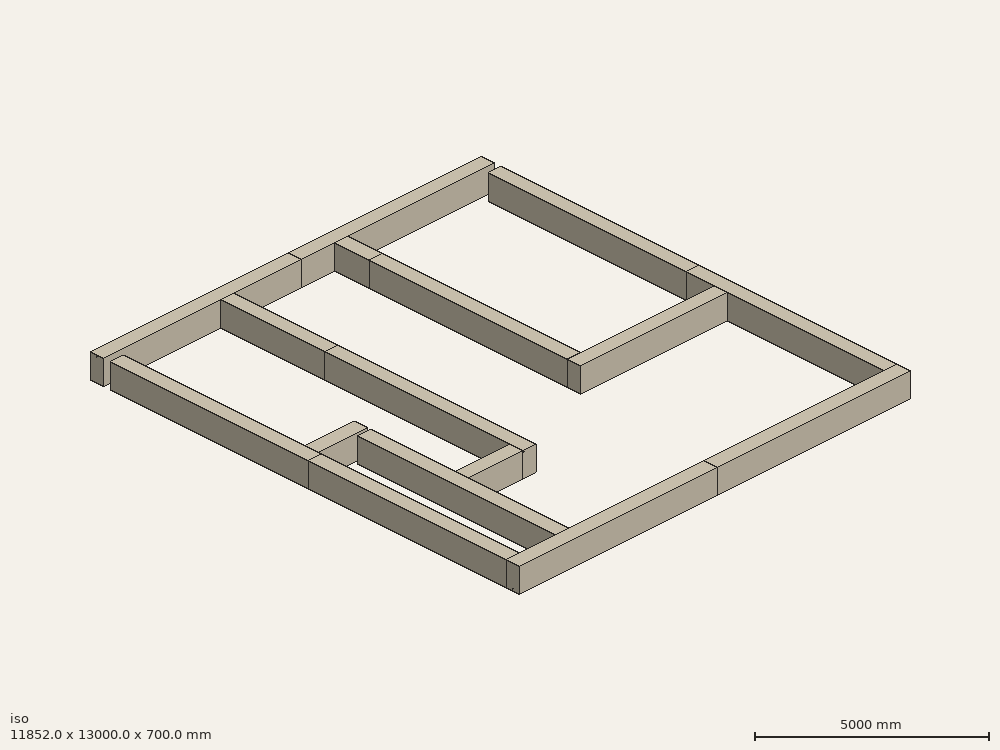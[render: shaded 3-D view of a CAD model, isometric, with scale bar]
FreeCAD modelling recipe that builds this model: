
FCSTD DOCUMENT  (FreeCAD 0.21R33668 +26 (Git))
Label: арматура
License: All rights reserved
objects: Part::FeaturePython×64, Sketcher::SketchObject×33, Part::Box×16, Part::Part2DObjectPython×16, Spreadsheet::Sheet×1
note: 129 computed .brp shape members not serialized (recipe doc carries the construction recipe); baked Part::Feature solids carry a one-line shape summary decoded from their .brp

FEATURE [Part::Box] Box  label="Куб"
  AttacherType = Attacher::AttachEngine3D
  Height = 700
  Length = 6000
  Width = 400
FEATURE [Part::FeaturePython] Structure  label="Структура"  # Arch/BIM 13 (typed FeaturePython)
  Base = -> Box
  BaseMirror = false
  BaseOffsetX = 0
  BaseOffsetY = 0
  BasePerpendicularToTool = false
  BaseRotation = 0
  ComputedLength = 0
  FaceMaker = 0
  Height = 4901.77
  HorizontalArea = 2400000
  IfcData = attributes={"GlobalId": {"name": "GlobalId", "type": "IfcGloballyUniqueId", "is_enum": false, "enum_values": []}, "Description": {"... (+484 chars omitted),+1 more (map truncated)
  IfcType = 13
  Length = 0
  MoveBase = false
  MoveWithHost = false
  NodesOffset = 0
  Normal = (0,0,0)
  PerimeterLength = 12800
  PredefinedType = 0
  ToolOffsetFirst = 0
  ToolOffsetLast = 0
  VerticalArea = 8960000
  Width = 500
FEATURE [Sketcher::SketchObject] Sketch
  FullyConstrained = false
  MapMode = 5
  Placement = pos=(0,0,0) rot=(1,0,0;1.5708rad)
  Support = -> [Structure]
  sketch-geometry (1):
    g0: LineSegment StartX=0 StartY=56 StartZ=0 EndX=6000 EndY=56 EndZ=0
FEATURE [Part::FeaturePython] Rebar  label="Нижняя_рабочая"  # Arch/BIM 110 (typed FeaturePython)
  Amount = 3
  AmountCheck = true
  Base = -> Sketch
  Cover = 50
  CoverAlong = Bottom Side
  Diameter = 12
  Direction = (0,0,0)
  Distance = 0
  FrontCover = 35
  HorizontalArea = 0
  Host = -> Structure
  IfcType = 110
  LeftBottomCover = 0
  Length = 6000
  Mark = StraightRebar
  MoveBase = false
  MoveWithHost = false
  OffsetEnd = 41
  OffsetStart = 41
  Orientation = Horizontal
  PerimeterLength = 0
  PlacementList = 3 placements: arithmetic series from (0,41,-9.10383e-15) step (0,159,-3.53051e-14) to (0,359,-7.9714e-14)
  RebarShape = 0
  RightTopCover = 0
  Rounding = 0
  Spacing = 159
  TotalLength = 18000
  TrueSpacing = 3
  VerticalArea = 0
FEATURE [Sketcher::SketchObject] Sketch001
  FullyConstrained = false
  MapMode = 5
  Placement = pos=(0,0,0) rot=(1,0,0;1.5708rad)
  Support = -> [Structure]
  sketch-geometry (1):
    g0: LineSegment StartX=0 StartY=659 StartZ=0 EndX=6000 EndY=659 EndZ=0
FEATURE [Part::FeaturePython] Rebar001  label="Верхняя_рабочая"  # Arch/BIM 110 (typed FeaturePython)
  Amount = 3
  AmountCheck = true
  Base = -> Sketch001
  Cover = 35
  CoverAlong = Top Side
  Diameter = 12
  Direction = (0,0,0)
  Distance = 0
  FrontCover = 35
  HorizontalArea = 0
  Host = -> Structure
  IfcType = 110
  LeftBottomCover = 0
  Length = 6000
  Mark = StraightRebar001
  MoveBase = false
  MoveWithHost = false
  OffsetEnd = 41
  OffsetStart = 41
  Orientation = Horizontal
  PerimeterLength = 0
  PlacementList = 3 placements: arithmetic series from (0,41,-9.10383e-15) step (0,159,-3.53051e-14) to (0,359,-7.9714e-14)
  RebarShape = 0
  RightTopCover = 0
  Rounding = 0
  Spacing = 159
  TotalLength = 18000
  TrueSpacing = 3
  VerticalArea = 0
FEATURE [Part::Part2DObjectPython] Wire  # Draft 2D object (typed FeaturePython)
  Area = 0
  ChamferSize = 0
  Closed = false
  End = (-10.6616,56.3137,621.059)
  FilletRadius = 0
  Length = 2124.59
  MakeFace = true
  Points = (7) [(2.13232,78.9411,643.686),(0,29,693.627),(-2.13232,29,44),(-4.26465,371,44),(-6.39697,371,671),(-8.5293,6.37258,671),(-10.6616,56.3137,621.059)]
  Start = (2.13232,78.9411,643.686)
  Subdivisions = 0
  Support = -> [Structure]
FEATURE [Part::FeaturePython] Rebar002  label="Хомуты"  # Arch/BIM 110 (typed FeaturePython)
  Amount = 13
  AmountCheck = false
  Base = -> Wire
  BentAngle = 135
  BentFactor = 4
  BottomCover = 40
  Diameter = 8
  Direction = (1,0,0)
  Distance = 0
  FrontCover = 80
  HorizontalArea = 0
  Host = -> Structure
  IfcType = 110
  LeftCover = 25
  Length = 2124.59
  Mark = Stirrup
  MoveBase = false
  MoveWithHost = false
  OffsetEnd = 84
  OffsetStart = 84
  PerimeterLength = 0
  PlacementList = 13 placements: arithmetic series from (84,0,0) step (485.333,0,0) to (5908,0,0)
  RebarShape = 3
  RightCover = 25
  Rounding = 2
  Spacing = 485.333
  TopCover = 25
  TotalLength = 27619.7
  TrueSpacing = 500
  VerticalArea = 0
FEATURE [Sketcher::SketchObject] Sketch003  label="контур_фундамента"
  FullyConstrained = true
  sketch-geometry (40):
    g0: LineSegment StartX=0 StartY=400 StartZ=0 EndX=11850 EndY=400 EndZ=0
    g1: LineSegment StartX=11850 StartY=400 StartZ=0 EndX=11850 EndY=0 EndZ=0
    g2: LineSegment StartX=11850 StartY=0 StartZ=0 EndX=0 EndY=0 EndZ=0
    g3: LineSegment StartX=0 StartY=0 StartZ=0 EndX=0 EndY=400 EndZ=0
    g4: LineSegment StartX=11850 StartY=13000 StartZ=0 EndX=11450 EndY=13000 EndZ=0
    g5: LineSegment StartX=11450 StartY=13000 StartZ=0 EndX=11450 EndY=0 EndZ=0
    g6: LineSegment StartX=11450 StartY=0 StartZ=0 EndX=11850 EndY=0 EndZ=0
    g7: LineSegment StartX=11850 StartY=0 StartZ=0 EndX=11850 EndY=13000 EndZ=0
    g8: LineSegment StartX=8.527e-13 StartY=13000 StartZ=0 EndX=11850 EndY=13000 EndZ=0
    g9: LineSegment StartX=11850 StartY=13000 StartZ=0 EndX=11850 EndY=12600 EndZ=0
    g10: LineSegment StartX=11850 StartY=12600 StartZ=0 EndX=0 EndY=12600 EndZ=0
    g11: LineSegment StartX=8.527e-13 StartY=12600 StartZ=0 EndX=8.527e-13 EndY=13000 EndZ=0
    g12: LineSegment StartX=8.527e-13 StartY=13000 StartZ=0 EndX=400 EndY=13000 EndZ=0
    g13: LineSegment StartX=400 StartY=13000 StartZ=0 EndX=400 EndY=1.819e-12 EndZ=0
    g14: LineSegment StartX=400 StartY=1.819e-12 StartZ=0 EndX=8.527e-13 EndY=1.819e-12 EndZ=0
    g15: LineSegment StartX=8.527e-13 StartY=1.819e-12 StartZ=0 EndX=8.527e-13 EndY=13000 EndZ=0
    g16: LineSegment StartX=3550 StartY=13000 StartZ=0 EndX=3950 EndY=13000 EndZ=0
    g17: LineSegment StartX=3950 StartY=13000 StartZ=0 EndX=3950 EndY=3450 EndZ=0
    g18: LineSegment StartX=3950 StartY=3450 StartZ=0 EndX=3550 EndY=3450 EndZ=0
    g19: LineSegment StartX=3550 StartY=3450 StartZ=0 EndX=3550 EndY=13000 EndZ=0
    g20: LineSegment StartX=9.095e-13 StartY=6900 StartZ=0 EndX=1900 EndY=6900 EndZ=0
    g21: LineSegment StartX=1900 StartY=6900 StartZ=0 EndX=1900 EndY=6500 EndZ=0
    g22: LineSegment StartX=1900 StartY=6500 StartZ=0 EndX=9.095e-13 EndY=6500 EndZ=0
    g23: LineSegment StartX=9.095e-13 StartY=6500 StartZ=0 EndX=9.095e-13 EndY=6900 EndZ=0
    g24: LineSegment StartX=1500 StartY=6900 StartZ=0 EndX=1900 EndY=6900 EndZ=0
    g25: LineSegment StartX=1900 StartY=6900 StartZ=0 EndX=1900 EndY=0 EndZ=0
    g26: LineSegment StartX=1900 StartY=0 StartZ=0 EndX=1500 EndY=0 EndZ=0
    g27: LineSegment StartX=1500 StartY=0 StartZ=0 EndX=1500 EndY=6900 EndZ=0
    g28: LineSegment StartX=1900 StartY=3850 StartZ=0 EndX=3950 EndY=3850 EndZ=0
    g29: LineSegment StartX=3950 StartY=3850 StartZ=0 EndX=3950 EndY=3450 EndZ=0
    g30: LineSegment StartX=3950 StartY=3450 StartZ=0 EndX=1900 EndY=3450 EndZ=0
    g31: LineSegment StartX=1900 StartY=3450 StartZ=0 EndX=1900 EndY=3850 EndZ=0
    g32: LineSegment StartX=7000 StartY=13000 StartZ=0 EndX=7400 EndY=13000 EndZ=0
    g33: LineSegment StartX=7400 StartY=13000 StartZ=0 EndX=7400 EndY=5150 EndZ=0
    g34: LineSegment StartX=7400 StartY=5150 StartZ=0 EndX=7000 EndY=5150 EndZ=0
    g35: LineSegment StartX=7000 StartY=5150 StartZ=0 EndX=7000 EndY=13000 EndZ=0
    g36: LineSegment StartX=7000 StartY=5550 StartZ=0 EndX=11450 EndY=5550 EndZ=0
    g37: LineSegment StartX=11450 StartY=5550 StartZ=0 EndX=11450 EndY=5150 EndZ=0
    g38: LineSegment StartX=11450 StartY=5150 StartZ=0 EndX=7000 EndY=5150 EndZ=0
    g39: LineSegment StartX=7000 StartY=5150 StartZ=0 EndX=7000 EndY=5550 EndZ=0
  constraints (113):
    c: Coincident(g0,g1)
    c: Coincident(g1,g2)
    c: Coincident(g2,g3)
    c: Coincident(g3,g0)
    c: Horizontal(g0)
    c: Horizontal(g2)
    c: Vertical(g1)
    c: Vertical(g3)
    c: DistanceX(g2,g2) = 11850
    c: DistanceY(g1,g1) = 400
    c: Coincident(g2,g-1)
    c: Coincident(g4,g5)
    c: Coincident(g5,g6)
    c: Coincident(g6,g7)
    c: Coincident(g7,g4)
    c: Horizontal(g4)
    c: Horizontal(g6)
    c: Vertical(g5)
    c: Vertical(g7)
    c: DistanceX(g6,g6) = 400
    c: DistanceY(g5,g5) = 13000
    c: Coincident(g6,g1)
    c: Coincident(g8,g9)
    c: Coincident(g9,g10)
    c: Coincident(g10,g11)
    c: Coincident(g11,g8)
    c: Horizontal(g8)
    c: Horizontal(g10)
    c: Vertical(g9)
    c: Vertical(g11)
    c: DistanceY(g9,g9) = 400
    c: DistanceX(g8,g8) = 11850
    c: Coincident(g8,g4)
    c: Coincident(g12,g13)
    c: Coincident(g13,g14)
    c: Coincident(g14,g15)
    c: Coincident(g15,g12)
    c: Horizontal(g12)
    c: Horizontal(g14)
    c: Vertical(g13)
    c: Vertical(g15)
    c: DistanceX(g12,g12) = 400
    c: DistanceY(g15,g15) = 13000
    c: Coincident(g12,g8)
    c: Coincident(g16,g17)
    c: Coincident(g17,g18)
    c: Coincident(g18,g19)
    c: Coincident(g19,g16)
    c: Horizontal(g16)
    c: Horizontal(g18)
    c: Vertical(g17)
    c: Vertical(g19)
    c: DistanceX(g16,g16) = 400
    c: DistanceX(g8,g16) = 3950
    c: DistanceY(g17,g8) = 9550
    c: DistanceY(g19,g19) = 9550
    c: Coincident(g20,g21)
    c: Coincident(g21,g22)
    c: Coincident(g22,g23)
    c: Coincident(g23,g20)
    c: Horizontal(g20)
    c: Horizontal(g22)
    c: Vertical(g21)
    c: Vertical(g23)
    c: DistanceX(g20,g20) = 1900
    c: DistanceY(g23,g23) = 400
    c: DistanceY(g22,g8) = 6500
    c: DistanceX(g8,g20) = 1900
    c: Coincident(g24,g25)
    c: Coincident(g25,g26)
    c: Coincident(g26,g27)
    c: Coincident(g27,g24)
    c: Horizontal(g24)
    c: Horizontal(g26)
    c: Vertical(g25)
    c: Vertical(g27)
    c: DistanceX(g24,g24) = 400
    c: DistanceY(g25,g25) = 6900
    c: Coincident(g24,g20)
    c: Coincident(g28,g29)
    c: Coincident(g29,g30)
    c: Coincident(g30,g31)
    c: Coincident(g31,g28)
    c: Horizontal(g28)
    c: Horizontal(g30)
    c: Vertical(g29)
    c: Vertical(g31)
    c: DistanceY(g29,g29) = 400
    c: DistanceX(g28,g28) = 2050
    c: Coincident(g17,g29)
    c: Coincident(g32,g33)
    c: Coincident(g33,g34)
    c: Coincident(g34,g35)
    c: Coincident(g35,g32)
    c: Horizontal(g32)
    c: Horizontal(g34)
    c: Vertical(g33)
    c: Vertical(g35)
    c: DistanceX(g32,g32) = 400
    c: DistanceY(g33,g33) = 7850
    c: DistanceX(g32,g4) = 4850
    c: DistanceY(g33,g4) = 7850
    c: Coincident(g36,g37)
    c: Coincident(g37,g38)
    c: Coincident(g38,g39)
    c: Coincident(g39,g36)
    c: Horizontal(g36)
    c: Horizontal(g38)
    c: Vertical(g37)
    c: Vertical(g39)
    c: DistanceY(g39,g39) = 400
    c: DistanceX(g38,g38) = 4450
    c: Coincident(g38,g34)
FEATURE [Part::Box] Box001  label="Куб001"
  AttacherType = Attacher::AttachEngine3D
  Height = 700
  Length = 5850
  Width = 400
FEATURE [Part::FeaturePython] Structure001  label="Структура001"  # Arch/BIM 13 (typed FeaturePython)
  Base = -> Box001
  BaseMirror = false
  BaseOffsetX = 0
  BaseOffsetY = 0
  BasePerpendicularToTool = false
  BaseRotation = 0
  ComputedLength = 0
  FaceMaker = 0
  Height = 345.39
  HorizontalArea = 2340000
  IfcData = attributes={"GlobalId": {"name": "GlobalId", "type": "IfcGloballyUniqueId", "is_enum": false, "enum_values": []}, "Description": {"... (+484 chars omitted),+1 more (map truncated)
  IfcType = 13
  Length = 0
  MoveBase = false
  MoveWithHost = false
  NodesOffset = 0
  Normal = (0,0,0)
  PerimeterLength = 12500
  Placement = pos=(6001,0,0) rot=(0,0,1;0rad)
  PredefinedType = 0
  ToolOffsetFirst = 0
  ToolOffsetLast = 0
  VerticalArea = 8750000
  Width = 100
FEATURE [Sketcher::SketchObject] Sketch004
  FullyConstrained = false
  MapMode = 5
  Placement = pos=(6001,0,0) rot=(1,0,0;1.5708rad)
  Support = -> [Structure001]
  sketch-geometry (1):
    g0: LineSegment StartX=0 StartY=56 StartZ=0 EndX=5850 EndY=56 EndZ=0
FEATURE [Part::FeaturePython] Rebar004  label="Нижняя_рабочая001"  # Arch/BIM 110 (typed FeaturePython)
  Amount = 3
  AmountCheck = true
  Base = -> Sketch004
  Cover = 50
  CoverAlong = Bottom Side
  Diameter = 12
  Direction = (0,0,0)
  Distance = 0
  FrontCover = 35
  HorizontalArea = 0
  Host = -> Structure001
  IfcType = 110
  LeftBottomCover = 0
  Length = 5850
  Mark = StraightRebar
  MoveBase = false
  MoveWithHost = false
  OffsetEnd = 41
  OffsetStart = 41
  Orientation = Horizontal
  PerimeterLength = 0
  PlacementList = 3 placements: arithmetic series from (0,41,-9.10383e-15) step (0,159,-3.53051e-14) to (0,359,-7.9714e-14)
  RebarShape = 0
  RightTopCover = 0
  Rounding = 0
  Spacing = 159
  TotalLength = 17550
  TrueSpacing = 3
  VerticalArea = 0
FEATURE [Sketcher::SketchObject] Sketch005
  FullyConstrained = false
  MapMode = 5
  Placement = pos=(6001,0,0) rot=(1,0,0;1.5708rad)
  Support = -> [Structure001]
  sketch-geometry (1):
    g0: LineSegment StartX=0 StartY=659 StartZ=0 EndX=5850 EndY=659 EndZ=0
FEATURE [Part::FeaturePython] Rebar005  label="Верхняя_рабочая001"  # Arch/BIM 110 (typed FeaturePython)
  Amount = 3
  AmountCheck = true
  Base = -> Sketch005
  Cover = 35
  CoverAlong = Top Side
  Diameter = 12
  Direction = (0,0,0)
  Distance = 0
  FrontCover = 35
  HorizontalArea = 0
  Host = -> Structure001
  IfcType = 110
  LeftBottomCover = 0
  Length = 5850
  Mark = StraightRebar
  MoveBase = false
  MoveWithHost = false
  OffsetEnd = 41
  OffsetStart = 41
  Orientation = Horizontal
  PerimeterLength = 0
  PlacementList = 3 placements: arithmetic series from (0,41,-9.10383e-15) step (0,159,-3.53051e-14) to (0,359,-7.9714e-14)
  RebarShape = 0
  RightTopCover = 0
  Rounding = 0
  Spacing = 159
  TotalLength = 17550
  TrueSpacing = 3
  VerticalArea = 0
FEATURE [Part::Part2DObjectPython] Wire001  # Draft 2D object (typed FeaturePython)
  Area = 0
  ChamferSize = 0
  Closed = false
  End = (11840.3,56.3137,621.059)
  FilletRadius = 0
  Length = 2124.59
  MakeFace = true
  Points = (7) [(11853.1,78.9411,643.686),(11851,29,693.627),(11848.9,29,44),(11846.7,371,44),(11844.6,371,671),(11842.5,6.37258,671),(11840.3,56.3137,621.059)]
  Start = (11853.1,78.9411,643.686)
  Subdivisions = 0
  Support = -> [Structure001]
FEATURE [Part::FeaturePython] Rebar007  label="Хомуты001"  # Arch/BIM 110 (typed FeaturePython)
  Amount = 13
  AmountCheck = false
  Base = -> Wire001
  BentAngle = 135
  BentFactor = 4
  BottomCover = 40
  Diameter = 8
  Direction = (-1,0,0)
  Distance = 0
  FrontCover = 80
  HorizontalArea = 0
  Host = -> Structure001
  IfcType = 110
  LeftCover = 25
  Length = 2124.59
  Mark = Stirrup
  MoveBase = false
  MoveWithHost = false
  OffsetEnd = 84
  OffsetStart = 84
  PerimeterLength = 0
  PlacementList = 13 placements: arithmetic series from (-84,0,0) step (-472.833,0,0) to (-5758,0,0)
  RebarShape = 3
  RightCover = 25
  Rounding = 2
  Spacing = 472.833
  TopCover = 25
  TotalLength = 27619.7
  TrueSpacing = 500
  VerticalArea = 0
FEATURE [Part::Box] Box002  label="Куб002"
  AttacherType = Attacher::AttachEngine3D
  Height = 700
  Length = 6000
  Width = 400
FEATURE [Part::FeaturePython] Structure002  label="Структура002"  # Arch/BIM 13 (typed FeaturePython)
  Base = -> Box002
  BaseMirror = false
  BaseOffsetX = 0
  BaseOffsetY = 0
  BasePerpendicularToTool = false
  BaseRotation = 0
  ComputedLength = 0
  FaceMaker = 0
  Height = 1000
  HorizontalArea = 2400000
  IfcData = attributes={"GlobalId": {"name": "GlobalId", "type": "IfcGloballyUniqueId", "is_enum": false, "enum_values": []}, "Description": {"... (+484 chars omitted),+1 more (map truncated)
  IfcType = 13
  Length = 0
  MoveBase = false
  MoveWithHost = false
  NodesOffset = 0
  Normal = (0,0,0)
  PerimeterLength = 12800
  Placement = pos=(399,403,0) rot=(0,0,1;1.5708rad)
  PredefinedType = 0
  ToolOffsetFirst = 0
  ToolOffsetLast = 0
  VerticalArea = 8960000
  Width = 100
FEATURE [Sketcher::SketchObject] Sketch007
  FullyConstrained = false
  MapMode = 5
  Placement = pos=(-1,403,0) rot=(-0.57735,0.57735,0.57735;4.18879rad)
  Support = -> [Structure002]
  sketch-geometry (1):
    g0: LineSegment StartX=-6000 StartY=56 StartZ=0 EndX=0 EndY=56 EndZ=0
FEATURE [Part::FeaturePython] Rebar008  label="Нижняя_рабочая002"  # Arch/BIM 110 (typed FeaturePython)
  Amount = 3
  AmountCheck = true
  Base = -> Sketch007
  Cover = 50
  CoverAlong = Bottom Side
  Diameter = 12
  Direction = (0,0,0)
  Distance = 0
  FrontCover = 35
  HorizontalArea = 0
  Host = -> Structure002
  IfcType = 110
  LeftBottomCover = 0
  Length = 6000
  Mark = StraightRebar
  MoveBase = false
  MoveWithHost = false
  OffsetEnd = 41
  OffsetStart = 41
  Orientation = Horizontal
  PerimeterLength = 0
  PlacementList = 3 placements: arithmetic series from (41,-4.55191e-15,-4.55191e-15) step (159,-1.76525e-14,-1.76525e-14) to (359,-3.9857e-14,-3.9857e-14)
  RebarShape = 0
  RightTopCover = 0
  Rounding = 0
  Spacing = 159
  TotalLength = 18000
  TrueSpacing = 3
  VerticalArea = 0
FEATURE [Sketcher::SketchObject] Sketch008
  FullyConstrained = false
  MapMode = 5
  Placement = pos=(-1,403,0) rot=(-0.57735,0.57735,0.57735;4.18879rad)
  Support = -> [Structure002]
  sketch-geometry (1):
    g0: LineSegment StartX=-6000 StartY=659 StartZ=0 EndX=0 EndY=659 EndZ=0
FEATURE [Part::FeaturePython] Rebar009  label="Верхняя_рабочая002"  # Arch/BIM 110 (typed FeaturePython)
  Amount = 3
  AmountCheck = true
  Base = -> Sketch008
  Cover = 35
  CoverAlong = Top Side
  Diameter = 12
  Direction = (0,0,0)
  Distance = 0
  FrontCover = 35
  HorizontalArea = 0
  Host = -> Structure002
  IfcType = 110
  LeftBottomCover = 0
  Length = 6000
  Mark = StraightRebar
  MoveBase = false
  MoveWithHost = false
  OffsetEnd = 41
  OffsetStart = 41
  Orientation = Horizontal
  PerimeterLength = 0
  PlacementList = 3 placements: arithmetic series from (41,-4.55191e-15,-4.55191e-15) step (159,-1.76525e-14,-1.76525e-14) to (359,-3.9857e-14,-3.9857e-14)
  RebarShape = 0
  RightTopCover = 0
  Rounding = 0
  Spacing = 159
  TotalLength = 18000
  TrueSpacing = 3
  VerticalArea = 0
FEATURE [Part::Part2DObjectPython] Wire002  # Draft 2D object (typed FeaturePython)
  Area = 0
  ChamferSize = 0
  Closed = false
  End = (55.3137,6392.34,621.059)
  FilletRadius = 0
  Length = 2124.59
  MakeFace = true
  Points = (7) [(77.9411,6405.13,643.686),(28,6403,693.627),(28,6400.87,44),(370,6398.74,44),(370,6396.6,671),(5.37258,6394.47,671),(55.3137,6392.34,621.059)]
  Start = (77.9411,6405.13,643.686)
  Subdivisions = 0
  Support = -> [Structure002]
FEATURE [Part::FeaturePython] Rebar011  label="Хомуты002"  # Arch/BIM 110 (typed FeaturePython)
  Amount = 13
  AmountCheck = false
  Base = -> Wire002
  BentAngle = 135
  BentFactor = 4
  BottomCover = 40
  Diameter = 8
  Direction = (-2e-16,-1,0)
  Distance = 0
  FrontCover = 80
  HorizontalArea = 0
  Host = -> Structure002
  IfcType = 110
  LeftCover = 25
  Length = 2124.59
  Mark = Stirrup
  MoveBase = false
  MoveWithHost = false
  OffsetEnd = 84
  OffsetStart = 84
  PerimeterLength = 0
  PlacementList = 13 placements: arithmetic series from (-1.86517e-14,-84,0) step (-1.07766e-13,-485.333,0) to (-1.31184e-12,-5908,0)
  RebarShape = 3
  RightCover = 25
  Rounding = 2
  Spacing = 485.333
  TopCover = 25
  TotalLength = 27619.7
  TrueSpacing = 500
  VerticalArea = 0
FEATURE [Part::Box] Box003  label="Куб003"
  AttacherType = Attacher::AttachEngine3D
  Height = 700
  Length = 6000
  Width = 400
FEATURE [Part::FeaturePython] Structure003  label="Структура003"  # Arch/BIM 13 (typed FeaturePython)
  Base = -> Box003
  BaseMirror = false
  BaseOffsetX = 0
  BaseOffsetY = 0
  BasePerpendicularToTool = false
  BaseRotation = 0
  ComputedLength = 0
  FaceMaker = 0
  Height = 1000
  HorizontalArea = 2400000
  IfcData = attributes={"GlobalId": {"name": "GlobalId", "type": "IfcGloballyUniqueId", "is_enum": false, "enum_values": []}, "Description": {"... (+484 chars omitted),+1 more (map truncated)
  IfcType = 13
  Length = 0
  MoveBase = false
  MoveWithHost = false
  NodesOffset = 0
  Normal = (0,0,0)
  PerimeterLength = 12800
  Placement = pos=(400,6403,0) rot=(0,0,1;1.5708rad)
  PredefinedType = 0
  ToolOffsetFirst = 0
  ToolOffsetLast = 0
  VerticalArea = 8960000
  Width = 100
FEATURE [Sketcher::SketchObject] Sketch010
  FullyConstrained = false
  MapMode = 5
  Placement = pos=(1.705e-13,6403,0) rot=(-0.57735,0.57735,0.57735;4.18879rad)
  Support = -> [Structure003]
  sketch-geometry (1):
    g0: LineSegment StartX=-6000 StartY=56 StartZ=0 EndX=0 EndY=56 EndZ=0
FEATURE [Part::FeaturePython] Rebar012  label="Нижняя_рабочая003"  # Arch/BIM 110 (typed FeaturePython)
  Amount = 3
  AmountCheck = true
  Base = -> Sketch010
  Cover = 50
  CoverAlong = Bottom Side
  Diameter = 12
  Direction = (0,0,0)
  Distance = 0
  FrontCover = 35
  HorizontalArea = 0
  Host = -> Structure003
  IfcType = 110
  LeftBottomCover = 0
  Length = 6000
  Mark = StraightRebar001
  MoveBase = false
  MoveWithHost = false
  OffsetEnd = 41
  OffsetStart = 41
  Orientation = Horizontal
  PerimeterLength = 0
  PlacementList = 3 placements: arithmetic series from (41,-4.55191e-15,-4.55191e-15) step (159,-1.76525e-14,-1.76525e-14) to (359,-3.9857e-14,-3.9857e-14)
  RebarShape = 0
  RightTopCover = 0
  Rounding = 0
  Spacing = 159
  TotalLength = 18000
  TrueSpacing = 3
  VerticalArea = 0
FEATURE [Sketcher::SketchObject] Sketch011
  FullyConstrained = false
  MapMode = 5
  Placement = pos=(1.705e-13,6403,0) rot=(-0.57735,0.57735,0.57735;4.18879rad)
  Support = -> [Structure003]
  sketch-geometry (1):
    g0: LineSegment StartX=-6000 StartY=659 StartZ=0 EndX=0 EndY=659 EndZ=0
FEATURE [Part::FeaturePython] Rebar013  label="Верхняя_рабочая003"  # Arch/BIM 110 (typed FeaturePython)
  Amount = 3
  AmountCheck = true
  Base = -> Sketch011
  Cover = 35
  CoverAlong = Top Side
  Diameter = 12
  Direction = (0,0,0)
  Distance = 0
  FrontCover = 35
  HorizontalArea = 0
  Host = -> Structure003
  IfcType = 110
  LeftBottomCover = 0
  Length = 6000
  Mark = StraightRebar001
  MoveBase = false
  MoveWithHost = false
  OffsetEnd = 41
  OffsetStart = 41
  Orientation = Horizontal
  PerimeterLength = 0
  PlacementList = 3 placements: arithmetic series from (41,-4.55191e-15,-4.55191e-15) step (159,-1.76525e-14,-1.76525e-14) to (359,-3.9857e-14,-3.9857e-14)
  RebarShape = 0
  RightTopCover = 0
  Rounding = 0
  Spacing = 159
  TotalLength = 18000
  TrueSpacing = 3
  VerticalArea = 0
FEATURE [Part::Part2DObjectPython] Wire003  # Draft 2D object (typed FeaturePython)
  Area = 0
  ChamferSize = 0
  Closed = false
  End = (56.3137,12392.3,621.059)
  FilletRadius = 0
  Length = 2124.59
  MakeFace = true
  Points = (7) [(78.9411,12405.1,643.686),(29,12403,693.627),(29,12400.9,44),(371,12398.7,44),(371,12396.6,671),(6.37258,12394.5,671),(56.3137,12392.3,621.059)]
  Start = (78.9411,12405.1,643.686)
  Subdivisions = 0
  Support = -> [Structure003]
FEATURE [Part::FeaturePython] Rebar015  label="Хомуты003"  # Arch/BIM 110 (typed FeaturePython)
  Amount = 13
  AmountCheck = false
  Base = -> Wire003
  BentAngle = 135
  BentFactor = 4
  BottomCover = 40
  Diameter = 8
  Direction = (-2e-16,-1,0)
  Distance = 0
  FrontCover = 80
  HorizontalArea = 0
  Host = -> Structure003
  IfcType = 110
  LeftCover = 25
  Length = 2124.59
  Mark = Stirrup
  MoveBase = false
  MoveWithHost = false
  OffsetEnd = 84
  OffsetStart = 84
  PerimeterLength = 0
  PlacementList = 13 placements: arithmetic series from (-1.86517e-14,-84,0) step (-1.07766e-13,-485.333,0) to (-1.31184e-12,-5908,0)
  RebarShape = 3
  RightCover = 25
  Rounding = 2
  Spacing = 485.333
  TopCover = 25
  TotalLength = 27619.7
  TrueSpacing = 500
  VerticalArea = 0
FEATURE [Part::Box] Box004  label="Куб004"
  AttacherType = Attacher::AttachEngine3D
  Height = 700
  Length = 6000
  Width = 400
FEATURE [Part::FeaturePython] Structure004  label="Структура004"  # Arch/BIM 13 (typed FeaturePython)
  Base = -> Box004
  BaseMirror = false
  BaseOffsetX = 0
  BaseOffsetY = 0
  BasePerpendicularToTool = false
  BaseRotation = 0
  ComputedLength = 0
  FaceMaker = 0
  Height = 1000
  HorizontalArea = 2400000
  IfcData = attributes={"GlobalId": {"name": "GlobalId", "type": "IfcGloballyUniqueId", "is_enum": false, "enum_values": []}, "Description": {"... (+484 chars omitted),+1 more (map truncated)
  IfcType = 13
  Length = 0
  MoveBase = false
  MoveWithHost = false
  NodesOffset = 0
  Normal = (0,0,0)
  PerimeterLength = 12800
  Placement = pos=(0,12600,0) rot=(0,0,1;0rad)
  PredefinedType = 0
  ToolOffsetFirst = 0
  ToolOffsetLast = 0
  VerticalArea = 8960000
  Width = 100
FEATURE [Sketcher::SketchObject] Sketch013
  FullyConstrained = false
  MapMode = 5
  Placement = pos=(0,13000,0) rot=(0,0.707107,0.707107;3.14159rad)
  Support = -> [Structure004]
  sketch-geometry (1):
    g0: LineSegment StartX=-6000 StartY=56 StartZ=0 EndX=0 EndY=56 EndZ=0
FEATURE [Part::FeaturePython] Rebar016  label="Нижняя_рабочая004"  # Arch/BIM 110 (typed FeaturePython)
  Amount = 3
  AmountCheck = true
  Base = -> Sketch013
  Cover = 50
  CoverAlong = Bottom Side
  Diameter = 12
  Direction = (0,0,0)
  Distance = 0
  FrontCover = 35
  HorizontalArea = 0
  Host = -> Structure004
  IfcType = 110
  LeftBottomCover = 0
  Length = 6000
  Mark = StraightRebar001
  MoveBase = false
  MoveWithHost = false
  OffsetEnd = 41
  OffsetStart = 41
  Orientation = Horizontal
  PerimeterLength = 0
  PlacementList = 3 placements: arithmetic series from (0,-41,9.10383e-15) step (0,-159,3.53051e-14) to (0,-359,7.9714e-14)
  RebarShape = 0
  RightTopCover = 0
  Rounding = 0
  Spacing = 159
  TotalLength = 18000
  TrueSpacing = 3
  VerticalArea = 0
FEATURE [Sketcher::SketchObject] Sketch014
  FullyConstrained = false
  MapMode = 5
  Placement = pos=(0,13000,0) rot=(0,0.707107,0.707107;3.14159rad)
  Support = -> [Structure004]
  sketch-geometry (1):
    g0: LineSegment StartX=-6000 StartY=659 StartZ=0 EndX=0 EndY=659 EndZ=0
FEATURE [Part::FeaturePython] Rebar017  label="Верхняя_рабочая004"  # Arch/BIM 110 (typed FeaturePython)
  Amount = 3
  AmountCheck = true
  Base = -> Sketch014
  Cover = 35
  CoverAlong = Top Side
  Diameter = 12
  Direction = (0,0,0)
  Distance = 0
  FrontCover = 35
  HorizontalArea = 0
  Host = -> Structure004
  IfcType = 110
  LeftBottomCover = 0
  Length = 6000
  Mark = StraightRebar002
  MoveBase = false
  MoveWithHost = false
  OffsetEnd = 41
  OffsetStart = 41
  Orientation = Horizontal
  PerimeterLength = 0
  PlacementList = 3 placements: arithmetic series from (0,-41,9.10383e-15) step (0,-159,3.53051e-14) to (0,-359,7.9714e-14)
  RebarShape = 0
  RightTopCover = 0
  Rounding = 0
  Spacing = 159
  TotalLength = 18000
  TrueSpacing = 3
  VerticalArea = 0
FEATURE [Part::Part2DObjectPython] Wire004  # Draft 2D object (typed FeaturePython)
  Area = 0
  ChamferSize = 0
  Closed = false
  End = (5989.34,12656.3,621.059)
  FilletRadius = 0
  Length = 2124.59
  MakeFace = true
  Points = (7) [(6002.13,12678.9,643.686),(6000,12629,693.627),(5997.87,12629,44),(5995.74,12971,44),(5993.6,12971,671),(5991.47,12606.4,671),(5989.34,12656.3,621.059)]
  Start = (6002.13,12678.9,643.686)
  Subdivisions = 0
  Support = -> [Structure004]
FEATURE [Part::FeaturePython] Rebar019  label="Хомуты004"  # Arch/BIM 110 (typed FeaturePython)
  Amount = 13
  AmountCheck = false
  Base = -> Wire004
  BentAngle = 135
  BentFactor = 4
  BottomCover = 40
  Diameter = 8
  Direction = (-1,0,0)
  Distance = 0
  FrontCover = 80
  HorizontalArea = 0
  Host = -> Structure004
  IfcType = 110
  LeftCover = 25
  Length = 2124.59
  Mark = Stirrup
  MoveBase = false
  MoveWithHost = false
  OffsetEnd = 84
  OffsetStart = 84
  PerimeterLength = 0
  PlacementList = 13 placements: arithmetic series from (-84,0,0) step (-485.333,0,0) to (-5908,0,0)
  RebarShape = 3
  RightCover = 25
  Rounding = 2
  Spacing = 485.333
  TopCover = 25
  TotalLength = 27619.7
  TrueSpacing = 500
  VerticalArea = 0
FEATURE [Part::Box] Box005  label="Куб005"
  AttacherType = Attacher::AttachEngine3D
  Height = 700
  Length = 5850
  Width = 400
FEATURE [Part::FeaturePython] Structure005  label="Структура005"  # Arch/BIM 13 (typed FeaturePython)
  Base = -> Box005
  BaseMirror = false
  BaseOffsetX = 0
  BaseOffsetY = 0
  BasePerpendicularToTool = false
  BaseRotation = 0
  ComputedLength = 0
  FaceMaker = 0
  Height = 1000
  HorizontalArea = 2340000
  IfcData = attributes={"GlobalId": {"name": "GlobalId", "type": "IfcGloballyUniqueId", "is_enum": false, "enum_values": []}, "Description": {"... (+484 chars omitted),+1 more (map truncated)
  IfcType = 13
  Length = 0
  MoveBase = false
  MoveWithHost = false
  NodesOffset = 0
  Normal = (0,0,0)
  PerimeterLength = 12500
  Placement = pos=(6001,12600,0) rot=(0,0,1;0rad)
  PredefinedType = 0
  ToolOffsetFirst = 0
  ToolOffsetLast = 0
  VerticalArea = 8750000
  Width = 100
FEATURE [Sketcher::SketchObject] Sketch016
  FullyConstrained = false
  MapMode = 5
  Placement = pos=(6001,13000,0) rot=(0,0.707107,0.707107;3.14159rad)
  Support = -> [Structure005]
  sketch-geometry (1):
    g0: LineSegment StartX=-5850 StartY=56 StartZ=0 EndX=0 EndY=56 EndZ=0
FEATURE [Part::FeaturePython] Rebar020  label="Нижняя_рабочая005"  # Arch/BIM 110 (typed FeaturePython)
  Amount = 3
  AmountCheck = true
  Base = -> Sketch016
  Cover = 50
  CoverAlong = Bottom Side
  Diameter = 12
  Direction = (0,0,0)
  Distance = 0
  FrontCover = 35
  HorizontalArea = 0
  Host = -> Structure005
  IfcType = 110
  LeftBottomCover = 0
  Length = 5850
  Mark = StraightRebar001
  MoveBase = false
  MoveWithHost = false
  OffsetEnd = 41
  OffsetStart = 41
  Orientation = Horizontal
  PerimeterLength = 0
  PlacementList = 3 placements: arithmetic series from (0,-41,9.10383e-15) step (0,-159,3.53051e-14) to (0,-359,7.9714e-14)
  RebarShape = 0
  RightTopCover = 0
  Rounding = 0
  Spacing = 159
  TotalLength = 17550
  TrueSpacing = 3
  VerticalArea = 0
FEATURE [Sketcher::SketchObject] Sketch017
  FullyConstrained = false
  MapMode = 5
  Placement = pos=(6001,13000,0) rot=(0,0.707107,0.707107;3.14159rad)
  Support = -> [Structure005]
  sketch-geometry (1):
    g0: LineSegment StartX=-5850 StartY=659 StartZ=0 EndX=0 EndY=659 EndZ=0
FEATURE [Part::FeaturePython] Rebar021  label="Верхняя_рабочая005"  # Arch/BIM 110 (typed FeaturePython)
  Amount = 3
  AmountCheck = true
  Base = -> Sketch017
  Cover = 35
  CoverAlong = Top Side
  Diameter = 12
  Direction = (0,0,0)
  Distance = 0
  FrontCover = 35
  HorizontalArea = 0
  Host = -> Structure005
  IfcType = 110
  LeftBottomCover = 0
  Length = 5850
  Mark = StraightRebar001
  MoveBase = false
  MoveWithHost = false
  OffsetEnd = 41
  OffsetStart = 41
  Orientation = Horizontal
  PerimeterLength = 0
  PlacementList = 3 placements: arithmetic series from (0,-41,9.10383e-15) step (0,-159,3.53051e-14) to (0,-359,7.9714e-14)
  RebarShape = 0
  RightTopCover = 0
  Rounding = 0
  Spacing = 159
  TotalLength = 17550
  TrueSpacing = 3
  VerticalArea = 0
FEATURE [Part::Part2DObjectPython] Wire005  # Draft 2D object (typed FeaturePython)
  Area = 0
  ChamferSize = 0
  Closed = false
  End = (11840.3,12656.3,621.059)
  FilletRadius = 0
  Length = 2124.59
  MakeFace = true
  Points = (7) [(11853.1,12678.9,643.686),(11851,12629,693.627),(11848.9,12629,44),(11846.7,12971,44),(11844.6,12971,671),(11842.5,12606.4,671),(11840.3,12656.3,621.059)]
  Start = (11853.1,12678.9,643.686)
  Subdivisions = 0
  Support = -> [Structure005]
FEATURE [Part::FeaturePython] Rebar023  label="Хомуты005"  # Arch/BIM 110 (typed FeaturePython)
  Amount = 13
  AmountCheck = false
  Base = -> Wire005
  BentAngle = 135
  BentFactor = 4
  BottomCover = 40
  Diameter = 8
  Direction = (-1,0,0)
  Distance = 0
  FrontCover = 80
  HorizontalArea = 0
  Host = -> Structure005
  IfcType = 110
  LeftCover = 25
  Length = 2124.59
  Mark = Stirrup
  MoveBase = false
  MoveWithHost = false
  OffsetEnd = 84
  OffsetStart = 84
  PerimeterLength = 0
  PlacementList = 13 placements: arithmetic series from (-84,0,0) step (-472.833,0,0) to (-5758,0,0)
  RebarShape = 3
  RightCover = 25
  Rounding = 2
  Spacing = 472.833
  TopCover = 25
  TotalLength = 27619.7
  TrueSpacing = 500
  VerticalArea = 0
FEATURE [Part::Box] Box006  label="Куб006"
  AttacherType = Attacher::AttachEngine3D
  Height = 700
  Length = 6000
  Width = 400
FEATURE [Part::FeaturePython] Structure006  label="Структура006"  # Arch/BIM 13 (typed FeaturePython)
  Base = -> Box006
  BaseMirror = false
  BaseOffsetX = 0
  BaseOffsetY = 0
  BasePerpendicularToTool = false
  BaseRotation = 0
  ComputedLength = 0
  FaceMaker = 0
  Height = 1000
  HorizontalArea = 2400000
  IfcData = attributes={"GlobalId": {"name": "GlobalId", "type": "IfcGloballyUniqueId", "is_enum": false, "enum_values": []}, "Description": {"... (+484 chars omitted),+1 more (map truncated)
  IfcType = 13
  Length = 0
  MoveBase = false
  MoveWithHost = false
  NodesOffset = 0
  Normal = (0,0,0)
  PerimeterLength = 12800
  Placement = pos=(11849,400,0) rot=(0,0,1;1.5708rad)
  PredefinedType = 0
  ToolOffsetFirst = 0
  ToolOffsetLast = 0
  VerticalArea = 8960000
  Width = 100
FEATURE [Sketcher::SketchObject] Sketch019
  FullyConstrained = false
  MapMode = 5
  Placement = pos=(11849,400,0) rot=(0.57735,0.57735,0.57735;2.0944rad)
  Support = -> [Structure006]
  sketch-geometry (1):
    g0: LineSegment StartX=-4.547e-13 StartY=56 StartZ=0 EndX=6000 EndY=56 EndZ=0
FEATURE [Part::FeaturePython] Rebar024  label="Нижняя_рабочая006"  # Arch/BIM 110 (typed FeaturePython)
  Amount = 3
  AmountCheck = true
  Base = -> Sketch019
  Cover = 50
  CoverAlong = Bottom Side
  Diameter = 12
  Direction = (0,0,0)
  Distance = 0
  FrontCover = 35
  HorizontalArea = 0
  Host = -> Structure006
  IfcType = 110
  LeftBottomCover = 0
  Length = 6000
  Mark = StraightRebar001
  MoveBase = false
  MoveWithHost = false
  OffsetEnd = 41
  OffsetStart = 41
  Orientation = Horizontal
  PerimeterLength = 0
  PlacementList = 3 placements: arithmetic series from (-41,4.55191e-15,4.55191e-15) step (-159,1.76525e-14,1.76525e-14) to (-359,3.9857e-14,3.9857e-14)
  RebarShape = 0
  RightTopCover = 0
  Rounding = 0
  Spacing = 159
  TotalLength = 18000
  TrueSpacing = 3
  VerticalArea = 0
FEATURE [Sketcher::SketchObject] Sketch020
  FullyConstrained = false
  MapMode = 5
  Placement = pos=(11849,400,0) rot=(0.57735,0.57735,0.57735;2.0944rad)
  Support = -> [Structure006]
  sketch-geometry (1):
    g0: LineSegment StartX=-4.547e-13 StartY=659 StartZ=0 EndX=6000 EndY=659 EndZ=0
FEATURE [Part::FeaturePython] Rebar025  label="Верхняя_рабочая006"  # Arch/BIM 110 (typed FeaturePython)
  Amount = 3
  AmountCheck = true
  Base = -> Sketch020
  Cover = 35
  CoverAlong = Top Side
  Diameter = 12
  Direction = (0,0,0)
  Distance = 0
  FrontCover = 35
  HorizontalArea = 0
  Host = -> Structure006
  IfcType = 110
  LeftBottomCover = 0
  Length = 6000
  Mark = StraightRebar001
  MoveBase = false
  MoveWithHost = false
  OffsetEnd = 41
  OffsetStart = 41
  Orientation = Horizontal
  PerimeterLength = 0
  PlacementList = 3 placements: arithmetic series from (-41,4.55191e-15,4.55191e-15) step (-159,1.76525e-14,1.76525e-14) to (-359,3.9857e-14,3.9857e-14)
  RebarShape = 0
  RightTopCover = 0
  Rounding = 0
  Spacing = 159
  TotalLength = 18000
  TrueSpacing = 3
  VerticalArea = 0
FEATURE [Part::Part2DObjectPython] Wire006  # Draft 2D object (typed FeaturePython)
  Area = 0
  ChamferSize = 0
  Closed = false
  End = (11505.3,6389.34,621.059)
  FilletRadius = 0
  Length = 2124.59
  MakeFace = true
  Points = (7) [(11527.9,6402.13,643.686),(11478,6400,693.627),(11478,6397.87,44),(11820,6395.74,44),(11820,6393.6,671),(11455.4,6391.47,671),(11505.3,6389.34,621.059)]
  Start = (11527.9,6402.13,643.686)
  Subdivisions = 0
  Support = -> [Structure006]
FEATURE [Part::FeaturePython] Rebar027  label="Хомуты006"  # Arch/BIM 110 (typed FeaturePython)
  Amount = 13
  AmountCheck = false
  Base = -> Wire006
  BentAngle = 135
  BentFactor = 4
  BottomCover = 40
  Diameter = 8
  Direction = (-2e-16,-1,0)
  Distance = 0
  FrontCover = 80
  HorizontalArea = 0
  Host = -> Structure006
  IfcType = 110
  LeftCover = 25
  Length = 2124.59
  Mark = Stirrup
  MoveBase = false
  MoveWithHost = false
  OffsetEnd = 84
  OffsetStart = 84
  PerimeterLength = 0
  PlacementList = 13 placements: arithmetic series from (-1.86517e-14,-84,0) step (-1.07766e-13,-485.333,0) to (-1.31184e-12,-5908,0)
  RebarShape = 3
  RightCover = 25
  Rounding = 2
  Spacing = 485.333
  TopCover = 25
  TotalLength = 27619.7
  TrueSpacing = 500
  VerticalArea = 0
FEATURE [Part::Box] Box007  label="Куб007"
  AttacherType = Attacher::AttachEngine3D
  Height = 700
  Length = 6000
  Width = 400
FEATURE [Part::FeaturePython] Structure007  label="Структура007"  # Arch/BIM 13 (typed FeaturePython)
  Base = -> Box007
  BaseMirror = false
  BaseOffsetX = 0
  BaseOffsetY = 0
  BasePerpendicularToTool = false
  BaseRotation = 0
  ComputedLength = 0
  FaceMaker = 0
  Height = 1000
  HorizontalArea = 2400000
  IfcData = attributes={"GlobalId": {"name": "GlobalId", "type": "IfcGloballyUniqueId", "is_enum": false, "enum_values": []}, "Description": {"... (+484 chars omitted),+1 more (map truncated)
  IfcType = 13
  Length = 0
  MoveBase = false
  MoveWithHost = false
  NodesOffset = 0
  Normal = (0,0,0)
  PerimeterLength = 12800
  Placement = pos=(11850,6402,0) rot=(0,0,1;1.5708rad)
  PredefinedType = 0
  ToolOffsetFirst = 0
  ToolOffsetLast = 0
  VerticalArea = 8960000
  Width = 100
FEATURE [Sketcher::SketchObject] Sketch022
  FullyConstrained = false
  MapMode = 5
  Placement = pos=(11850,6402,0) rot=(0.57735,0.57735,0.57735;2.0944rad)
  Support = -> [Structure007]
  sketch-geometry (1):
    g0: LineSegment StartX=0 StartY=56 StartZ=0 EndX=6000 EndY=56 EndZ=0
FEATURE [Part::FeaturePython] Rebar028  label="Нижняя_рабочая007"  # Arch/BIM 110 (typed FeaturePython)
  Amount = 3
  AmountCheck = true
  Base = -> Sketch022
  Cover = 50
  CoverAlong = Bottom Side
  Diameter = 12
  Direction = (0,0,0)
  Distance = 0
  FrontCover = 35
  HorizontalArea = 0
  Host = -> Structure007
  IfcType = 110
  LeftBottomCover = 0
  Length = 6000
  Mark = StraightRebar001
  MoveBase = false
  MoveWithHost = false
  OffsetEnd = 41
  OffsetStart = 41
  Orientation = Horizontal
  PerimeterLength = 0
  PlacementList = 3 placements: arithmetic series from (-41,4.55191e-15,4.55191e-15) step (-159,1.76525e-14,1.76525e-14) to (-359,3.9857e-14,3.9857e-14)
  RebarShape = 0
  RightTopCover = 0
  Rounding = 0
  Spacing = 159
  TotalLength = 18000
  TrueSpacing = 3
  VerticalArea = 0
FEATURE [Sketcher::SketchObject] Sketch023
  FullyConstrained = false
  MapMode = 5
  Placement = pos=(11850,6402,0) rot=(0.57735,0.57735,0.57735;2.0944rad)
  Support = -> [Structure007]
  sketch-geometry (1):
    g0: LineSegment StartX=0 StartY=659 StartZ=0 EndX=6000 EndY=659 EndZ=0
FEATURE [Part::FeaturePython] Rebar029  label="Верхняя_рабочая007"  # Arch/BIM 110 (typed FeaturePython)
  Amount = 3
  AmountCheck = true
  Base = -> Sketch023
  Cover = 35
  CoverAlong = Top Side
  Diameter = 12
  Direction = (0,0,0)
  Distance = 0
  FrontCover = 35
  HorizontalArea = 0
  Host = -> Structure007
  IfcType = 110
  LeftBottomCover = 0
  Length = 6000
  Mark = StraightRebar002
  MoveBase = false
  MoveWithHost = false
  OffsetEnd = 41
  OffsetStart = 41
  Orientation = Horizontal
  PerimeterLength = 0
  PlacementList = 3 placements: arithmetic series from (-41,4.55191e-15,4.55191e-15) step (-159,1.76525e-14,1.76525e-14) to (-359,3.9857e-14,3.9857e-14)
  RebarShape = 0
  RightTopCover = 0
  Rounding = 0
  Spacing = 159
  TotalLength = 18000
  TrueSpacing = 3
  VerticalArea = 0
FEATURE [Part::Part2DObjectPython] Wire007  # Draft 2D object (typed FeaturePython)
  Area = 0
  ChamferSize = 0
  Closed = false
  End = (11506.3,12391.3,621.059)
  FilletRadius = 0
  Length = 2124.59
  MakeFace = true
  Points = (7) [(11528.9,12404.1,643.686),(11479,12402,693.627),(11479,12399.9,44),(11821,12397.7,44),(11821,12395.6,671),(11456.4,12393.5,671),(11506.3,12391.3,621.059)]
  Start = (11528.9,12404.1,643.686)
  Subdivisions = 0
  Support = -> [Structure007]
FEATURE [Part::FeaturePython] Rebar031  label="Хомуты007"  # Arch/BIM 110 (typed FeaturePython)
  Amount = 13
  AmountCheck = false
  Base = -> Wire007
  BentAngle = 135
  BentFactor = 4
  BottomCover = 40
  Diameter = 8
  Direction = (-2e-16,-1,0)
  Distance = 0
  FrontCover = 80
  HorizontalArea = 0
  Host = -> Structure007
  IfcType = 110
  LeftCover = 25
  Length = 2124.59
  Mark = Stirrup
  MoveBase = false
  MoveWithHost = false
  OffsetEnd = 84
  OffsetStart = 84
  PerimeterLength = 0
  PlacementList = 13 placements: arithmetic series from (-1.86517e-14,-84,0) step (-1.07766e-13,-485.333,0) to (-1.31184e-12,-5908,0)
  RebarShape = 3
  RightCover = 25
  Rounding = 2
  Spacing = 485.333
  TopCover = 25
  TotalLength = 27619.7
  TrueSpacing = 500
  VerticalArea = 0
FEATURE [Part::Box] Box008  label="Куб008"
  AttacherType = Attacher::AttachEngine3D
  Height = 700
  Length = 6000
  Width = 400
FEATURE [Part::FeaturePython] Structure008  label="Структура008"  # Arch/BIM 13 (typed FeaturePython)
  Base = -> Box008
  BaseMirror = false
  BaseOffsetX = 0
  BaseOffsetY = 0
  BasePerpendicularToTool = false
  BaseRotation = 0
  ComputedLength = 0
  FaceMaker = 0
  Height = 1000
  HorizontalArea = 2400000
  IfcData = attributes={"GlobalId": {"name": "GlobalId", "type": "IfcGloballyUniqueId", "is_enum": false, "enum_values": []}, "Description": {"... (+484 chars omitted),+1 more (map truncated)
  IfcType = 13
  Length = 0
  MoveBase = false
  MoveWithHost = false
  NodesOffset = 0
  Normal = (0,0,0)
  PerimeterLength = 12800
  Placement = pos=(1900,400,0) rot=(0,0,1;1.5708rad)
  PredefinedType = 0
  ToolOffsetFirst = 0
  ToolOffsetLast = 0
  VerticalArea = 8960000
  Width = 100
FEATURE [Sketcher::SketchObject] Sketch025
  FullyConstrained = false
  MapMode = 5
  Placement = pos=(1500,400,0) rot=(-0.57735,0.57735,0.57735;4.18879rad)
  Support = -> [Structure008]
  sketch-geometry (1):
    g0: LineSegment StartX=-6000 StartY=56 StartZ=0 EndX=0 EndY=56 EndZ=0
FEATURE [Part::FeaturePython] Rebar032  label="Нижняя_рабочая008"  # Arch/BIM 110 (typed FeaturePython)
  Amount = 3
  AmountCheck = true
  Base = -> Sketch025
  Cover = 50
  CoverAlong = Bottom Side
  Diameter = 12
  Direction = (0,0,0)
  Distance = 0
  FrontCover = 35
  HorizontalArea = 0
  Host = -> Structure008
  IfcType = 110
  LeftBottomCover = 0
  Length = 6000
  Mark = StraightRebar001
  MoveBase = false
  MoveWithHost = false
  OffsetEnd = 41
  OffsetStart = 41
  Orientation = Horizontal
  PerimeterLength = 0
  PlacementList = 3 placements: arithmetic series from (41,-4.55191e-15,-4.55191e-15) step (159,-1.76525e-14,-1.76525e-14) to (359,-3.9857e-14,-3.9857e-14)
  RebarShape = 0
  RightTopCover = 0
  Rounding = 0
  Spacing = 159
  TotalLength = 18000
  TrueSpacing = 3
  VerticalArea = 0
FEATURE [Sketcher::SketchObject] Sketch026
  FullyConstrained = false
  MapMode = 5
  Placement = pos=(1500,400,0) rot=(-0.57735,0.57735,0.57735;4.18879rad)
  Support = -> [Structure008]
  sketch-geometry (1):
    g0: LineSegment StartX=-6000 StartY=659 StartZ=0 EndX=0 EndY=659 EndZ=0
FEATURE [Part::FeaturePython] Rebar033  label="Верхняя_рабочая008"  # Arch/BIM 110 (typed FeaturePython)
  Amount = 3
  AmountCheck = true
  Base = -> Sketch026
  Cover = 35
  CoverAlong = Top Side
  Diameter = 12
  Direction = (0,0,0)
  Distance = 0
  FrontCover = 35
  HorizontalArea = 0
  Host = -> Structure008
  IfcType = 110
  LeftBottomCover = 0
  Length = 6000
  Mark = StraightRebar001
  MoveBase = false
  MoveWithHost = false
  OffsetEnd = 41
  OffsetStart = 41
  Orientation = Horizontal
  PerimeterLength = 0
  PlacementList = 3 placements: arithmetic series from (41,-4.55191e-15,-4.55191e-15) step (159,-1.76525e-14,-1.76525e-14) to (359,-3.9857e-14,-3.9857e-14)
  RebarShape = 0
  RightTopCover = 0
  Rounding = 0
  Spacing = 159
  TotalLength = 18000
  TrueSpacing = 3
  VerticalArea = 0
FEATURE [Part::Part2DObjectPython] Wire008  # Draft 2D object (typed FeaturePython)
  Area = 0
  ChamferSize = 0
  Closed = false
  End = (1556.31,6389.34,621.059)
  FilletRadius = 0
  Length = 2124.59
  MakeFace = true
  Points = (7) [(1578.94,6402.13,643.686),(1529,6400,693.627),(1529,6397.87,44),(1871,6395.74,44),(1871,6393.6,671),(1506.37,6391.47,671),(1556.31,6389.34,621.059)]
  Start = (1578.94,6402.13,643.686)
  Subdivisions = 0
  Support = -> [Structure008]
FEATURE [Part::FeaturePython] Rebar035  label="Хомуты008"  # Arch/BIM 110 (typed FeaturePython)
  Amount = 13
  AmountCheck = false
  Base = -> Wire008
  BentAngle = 135
  BentFactor = 4
  BottomCover = 40
  Diameter = 8
  Direction = (-2e-16,-1,0)
  Distance = 0
  FrontCover = 80
  HorizontalArea = 0
  Host = -> Structure008
  IfcType = 110
  LeftCover = 25
  Length = 2124.59
  Mark = Stirrup
  MoveBase = false
  MoveWithHost = false
  OffsetEnd = 84
  OffsetStart = 84
  PerimeterLength = 0
  PlacementList = 13 placements: arithmetic series from (-1.86517e-14,-84,0) step (-1.07766e-13,-485.333,0) to (-1.31184e-12,-5908,0)
  RebarShape = 3
  RightCover = 25
  Rounding = 2
  Spacing = 485.333
  TopCover = 25
  TotalLength = 27619.7
  TrueSpacing = 500
  VerticalArea = 0
FEATURE [Part::Box] Box009  label="Куб009"
  AttacherType = Attacher::AttachEngine3D
  Height = 700
  Length = 1500
  Width = 400
FEATURE [Part::FeaturePython] Structure009  label="Структура009"  # Arch/BIM 13 (typed FeaturePython)
  Base = -> Box009
  BaseMirror = false
  BaseOffsetX = 0
  BaseOffsetY = 0
  BasePerpendicularToTool = false
  BaseRotation = 0
  ComputedLength = 0
  FaceMaker = 0
  Height = 1000
  HorizontalArea = 600000
  IfcData = attributes={"GlobalId": {"name": "GlobalId", "type": "IfcGloballyUniqueId", "is_enum": false, "enum_values": []}, "Description": {"... (+484 chars omitted),+1 more (map truncated)
  IfcType = 13
  Length = 0
  MoveBase = false
  MoveWithHost = false
  NodesOffset = 0
  Normal = (0,0,0)
  PerimeterLength = 3800
  Placement = pos=(400,6501,0) rot=(0,0,1;0rad)
  PredefinedType = 0
  ToolOffsetFirst = 0
  ToolOffsetLast = 0
  VerticalArea = 2660000
  Width = 100
FEATURE [Sketcher::SketchObject] Sketch028
  FullyConstrained = false
  MapMode = 5
  Placement = pos=(400,6501,0) rot=(1,0,0;1.5708rad)
  Support = -> [Structure009]
  sketch-geometry (1):
    g0: LineSegment StartX=0 StartY=56 StartZ=0 EndX=1500 EndY=56 EndZ=0
FEATURE [Part::FeaturePython] Rebar036  label="Нижняя_рабочая009"  # Arch/BIM 110 (typed FeaturePython)
  Amount = 3
  AmountCheck = true
  Base = -> Sketch028
  Cover = 50
  CoverAlong = Bottom Side
  Diameter = 12
  Direction = (0,0,0)
  Distance = 0
  FrontCover = 35
  HorizontalArea = 0
  Host = -> Structure009
  IfcType = 110
  LeftBottomCover = 0
  Length = 1500
  Mark = StraightRebar001
  MoveBase = false
  MoveWithHost = false
  OffsetEnd = 41
  OffsetStart = 41
  Orientation = Horizontal
  PerimeterLength = 0
  PlacementList = 3 placements: arithmetic series from (0,41,-9.10383e-15) step (0,159,-3.53051e-14) to (0,359,-7.9714e-14)
  RebarShape = 0
  RightTopCover = 0
  Rounding = 0
  Spacing = 159
  TotalLength = 4500
  TrueSpacing = 3
  VerticalArea = 0
FEATURE [Sketcher::SketchObject] Sketch029
  FullyConstrained = false
  MapMode = 5
  Placement = pos=(400,6501,0) rot=(1,0,0;1.5708rad)
  Support = -> [Structure009]
  sketch-geometry (1):
    g0: LineSegment StartX=0 StartY=659 StartZ=0 EndX=1500 EndY=659 EndZ=0
FEATURE [Part::FeaturePython] Rebar037  label="Верхняя_рабочая009"  # Arch/BIM 110 (typed FeaturePython)
  Amount = 3
  AmountCheck = true
  Base = -> Sketch029
  Cover = 35
  CoverAlong = Top Side
  Diameter = 12
  Direction = (0,0,0)
  Distance = 0
  FrontCover = 35
  HorizontalArea = 0
  Host = -> Structure009
  IfcType = 110
  LeftBottomCover = 0
  Length = 1500
  Mark = StraightRebar001
  MoveBase = false
  MoveWithHost = false
  OffsetEnd = 41
  OffsetStart = 41
  Orientation = Horizontal
  PerimeterLength = 0
  PlacementList = 3 placements: arithmetic series from (0,41,-9.10383e-15) step (0,159,-3.53051e-14) to (0,359,-7.9714e-14)
  RebarShape = 0
  RightTopCover = 0
  Rounding = 0
  Spacing = 159
  TotalLength = 4500
  TrueSpacing = 3
  VerticalArea = 0
FEATURE [Part::Part2DObjectPython] Wire009  # Draft 2D object (typed FeaturePython)
  Area = 0
  ChamferSize = 0
  Closed = false
  End = (1889.34,6557.31,621.059)
  FilletRadius = 0
  Length = 2124.59
  MakeFace = true
  Points = (7) [(1902.13,6579.94,643.686),(1900,6530,693.627),(1897.87,6530,44),(1895.74,6872,44),(1893.6,6872,671),(1891.47,6507.37,671),(1889.34,6557.31,621.059)]
  Start = (1902.13,6579.94,643.686)
  Subdivisions = 0
  Support = -> [Structure009]
FEATURE [Part::FeaturePython] Rebar039  label="Хомуты009"  # Arch/BIM 110 (typed FeaturePython)
  Amount = 4
  AmountCheck = false
  Base = -> Wire009
  BentAngle = 135
  BentFactor = 4
  BottomCover = 40
  Diameter = 8
  Direction = (-1,0,0)
  Distance = 0
  FrontCover = 80
  HorizontalArea = 0
  Host = -> Structure009
  IfcType = 110
  LeftCover = 25
  Length = 2124.59
  Mark = Stirrup
  MoveBase = false
  MoveWithHost = false
  OffsetEnd = 84
  OffsetStart = 84
  PerimeterLength = 0
  PlacementList = 4 placements: arithmetic series from (-84,0,0) step (-441.333,0,0) to (-1408,0,0)
  RebarShape = 3
  RightCover = 25
  Rounding = 2
  Spacing = 441.333
  TopCover = 25
  TotalLength = 8498.38
  TrueSpacing = 500
  VerticalArea = 0
FEATURE [Part::Box] Box010  label="Куб010"
  AttacherType = Attacher::AttachEngine3D
  Height = 700
  Length = 6000
  Width = 400
FEATURE [Part::FeaturePython] Structure010  label="Структура010"  # Arch/BIM 13 (typed FeaturePython)
  Base = -> Box010
  BaseMirror = false
  BaseOffsetX = 0
  BaseOffsetY = 0
  BasePerpendicularToTool = false
  BaseRotation = 0
  ComputedLength = 0
  FaceMaker = 0
  Height = 1000
  HorizontalArea = 2400000
  IfcData = attributes={"GlobalId": {"name": "GlobalId", "type": "IfcGloballyUniqueId", "is_enum": false, "enum_values": []}, "Description": {"... (+484 chars omitted),+1 more (map truncated)
  IfcType = 13
  Length = 0
  MoveBase = false
  MoveWithHost = false
  NodesOffset = 0
  Normal = (0,0,0)
  PerimeterLength = 12800
  Placement = pos=(3952,3450,0) rot=(0,0,1;1.5708rad)
  PredefinedType = 0
  ToolOffsetFirst = 0
  ToolOffsetLast = 0
  VerticalArea = 8960000
  Width = 100
FEATURE [Sketcher::SketchObject] Sketch031
  FullyConstrained = false
  MapMode = 5
  Placement = pos=(3952,3450,0) rot=(0.57735,0.57735,0.57735;2.0944rad)
  Support = -> [Structure010]
  sketch-geometry (1):
    g0: LineSegment StartX=0 StartY=56 StartZ=0 EndX=6000 EndY=56 EndZ=0
FEATURE [Part::FeaturePython] Rebar040  label="Нижняя_рабочая010"  # Arch/BIM 110 (typed FeaturePython)
  Amount = 3
  AmountCheck = true
  Base = -> Sketch031
  Cover = 50
  CoverAlong = Bottom Side
  Diameter = 12
  Direction = (0,0,0)
  Distance = 0
  FrontCover = 35
  HorizontalArea = 0
  Host = -> Structure010
  IfcType = 110
  LeftBottomCover = 0
  Length = 6000
  Mark = StraightRebar001
  MoveBase = false
  MoveWithHost = false
  OffsetEnd = 41
  OffsetStart = 41
  Orientation = Horizontal
  PerimeterLength = 0
  PlacementList = 3 placements: arithmetic series from (-41,4.55191e-15,4.55191e-15) step (-159,1.76525e-14,1.76525e-14) to (-359,3.9857e-14,3.9857e-14)
  RebarShape = 0
  RightTopCover = 0
  Rounding = 0
  Spacing = 159
  TotalLength = 18000
  TrueSpacing = 3
  VerticalArea = 0
FEATURE [Sketcher::SketchObject] Sketch032
  FullyConstrained = false
  MapMode = 5
  Placement = pos=(3952,3450,0) rot=(0.57735,0.57735,0.57735;2.0944rad)
  Support = -> [Structure010]
  sketch-geometry (1):
    g0: LineSegment StartX=0 StartY=659 StartZ=0 EndX=6000 EndY=659 EndZ=0
FEATURE [Part::FeaturePython] Rebar041  label="Верхняя_рабочая010"  # Arch/BIM 110 (typed FeaturePython)
  Amount = 3
  AmountCheck = true
  Base = -> Sketch032
  Cover = 35
  CoverAlong = Top Side
  Diameter = 12
  Direction = (0,0,0)
  Distance = 0
  FrontCover = 35
  HorizontalArea = 0
  Host = -> Structure010
  IfcType = 110
  LeftBottomCover = 0
  Length = 6000
  Mark = StraightRebar001
  MoveBase = false
  MoveWithHost = false
  OffsetEnd = 41
  OffsetStart = 41
  Orientation = Horizontal
  PerimeterLength = 0
  PlacementList = 3 placements: arithmetic series from (-41,4.55191e-15,4.55191e-15) step (-159,1.76525e-14,1.76525e-14) to (-359,3.9857e-14,3.9857e-14)
  RebarShape = 0
  RightTopCover = 0
  Rounding = 0
  Spacing = 159
  TotalLength = 18000
  TrueSpacing = 3
  VerticalArea = 0
FEATURE [Part::Part2DObjectPython] Wire010  # Draft 2D object (typed FeaturePython)
  Area = 0
  ChamferSize = 0
  Closed = false
  End = (3608.31,3439.34,621.059)
  FilletRadius = 0
  Length = 2124.59
  MakeFace = true
  Points = (7) [(3630.94,3452.13,643.686),(3581,3450,693.627),(3581,3447.87,44),(3923,3445.74,44),(3923,3443.6,671),(3558.37,3441.47,671),(3608.31,3439.34,621.059)]
  Start = (3630.94,3452.13,643.686)
  Subdivisions = 0
  Support = -> [Structure010]
FEATURE [Part::FeaturePython] Rebar043  label="Хомуты010"  # Arch/BIM 110 (typed FeaturePython)
  Amount = 13
  AmountCheck = false
  Base = -> Wire010
  BentAngle = 135
  BentFactor = 4
  BottomCover = 40
  Diameter = 8
  Direction = (2e-16,1,0)
  Distance = 0
  FrontCover = 80
  HorizontalArea = 0
  Host = -> Structure010
  IfcType = 110
  LeftCover = 25
  Length = 2124.59
  Mark = Stirrup
  MoveBase = false
  MoveWithHost = false
  OffsetEnd = 84
  OffsetStart = 84
  PerimeterLength = 0
  PlacementList = 13 placements: arithmetic series from (1.86517e-14,84,0) step (1.07766e-13,485.333,0) to (1.31184e-12,5908,0)
  RebarShape = 3
  RightCover = 25
  Rounding = 2
  Spacing = 485.333
  TopCover = 25
  TotalLength = 27619.7
  TrueSpacing = 500
  VerticalArea = 0
FEATURE [Part::Box] Box011  label="Куб011"
  AttacherType = Attacher::AttachEngine3D
  Height = 700
  Length = 6000
  Width = 400
FEATURE [Part::FeaturePython] Structure011  label="Структура011"  # Arch/BIM 13 (typed FeaturePython)
  Base = -> Box011
  BaseMirror = false
  BaseOffsetX = 0
  BaseOffsetY = 0
  BasePerpendicularToTool = false
  BaseRotation = 0
  ComputedLength = 0
  FaceMaker = 0
  Height = 1000
  HorizontalArea = 2400000
  IfcData = attributes={"GlobalId": {"name": "GlobalId", "type": "IfcGloballyUniqueId", "is_enum": false, "enum_values": []}, "Description": {"... (+484 chars omitted),+1 more (map truncated)
  IfcType = 13
  Length = 0
  MoveBase = false
  MoveWithHost = false
  NodesOffset = 0
  Normal = (0,0,0)
  PerimeterLength = 12800
  Placement = pos=(7400,5550,0) rot=(0,0,1;1.5708rad)
  PredefinedType = 0
  ToolOffsetFirst = 0
  ToolOffsetLast = 0
  VerticalArea = 8960000
  Width = 100
FEATURE [Sketcher::SketchObject] Sketch034
  FullyConstrained = false
  MapMode = 5
  Placement = pos=(7400,5550,0) rot=(0.57735,0.57735,0.57735;2.0944rad)
  Support = -> [Structure011]
  sketch-geometry (1):
    g0: LineSegment StartX=0 StartY=56 StartZ=0 EndX=6000 EndY=56 EndZ=0
FEATURE [Part::FeaturePython] Rebar044  label="Нижняя_рабочая011"  # Arch/BIM 110 (typed FeaturePython)
  Amount = 3
  AmountCheck = true
  Base = -> Sketch034
  Cover = 50
  CoverAlong = Bottom Side
  Diameter = 12
  Direction = (0,0,0)
  Distance = 0
  FrontCover = 35
  HorizontalArea = 0
  Host = -> Structure011
  IfcType = 110
  LeftBottomCover = 0
  Length = 6000
  Mark = StraightRebar001
  MoveBase = false
  MoveWithHost = false
  OffsetEnd = 41
  OffsetStart = 41
  Orientation = Horizontal
  PerimeterLength = 0
  PlacementList = 3 placements: arithmetic series from (-41,4.55191e-15,4.55191e-15) step (-159,1.76525e-14,1.76525e-14) to (-359,3.9857e-14,3.9857e-14)
  RebarShape = 0
  RightTopCover = 0
  Rounding = 0
  Spacing = 159
  TotalLength = 18000
  TrueSpacing = 3
  VerticalArea = 0
FEATURE [Sketcher::SketchObject] Sketch035
  FullyConstrained = false
  MapMode = 5
  Placement = pos=(7400,5550,0) rot=(0.57735,0.57735,0.57735;2.0944rad)
  Support = -> [Structure011]
  sketch-geometry (1):
    g0: LineSegment StartX=0 StartY=659 StartZ=0 EndX=6000 EndY=659 EndZ=0
FEATURE [Part::FeaturePython] Rebar045  label="Верхняя_рабочая011"  # Arch/BIM 110 (typed FeaturePython)
  Amount = 3
  AmountCheck = true
  Base = -> Sketch035
  Cover = 35
  CoverAlong = Top Side
  Diameter = 12
  Direction = (0,0,0)
  Distance = 0
  FrontCover = 35
  HorizontalArea = 0
  Host = -> Structure011
  IfcType = 110
  LeftBottomCover = 0
  Length = 6000
  Mark = StraightRebar001
  MoveBase = false
  MoveWithHost = false
  OffsetEnd = 41
  OffsetStart = 41
  Orientation = Horizontal
  PerimeterLength = 0
  PlacementList = 3 placements: arithmetic series from (-41,4.55191e-15,4.55191e-15) step (-159,1.76525e-14,1.76525e-14) to (-359,3.9857e-14,3.9857e-14)
  RebarShape = 0
  RightTopCover = 0
  Rounding = 0
  Spacing = 159
  TotalLength = 18000
  TrueSpacing = 3
  VerticalArea = 0
FEATURE [Part::Part2DObjectPython] Wire011  # Draft 2D object (typed FeaturePython)
  Area = 0
  ChamferSize = 0
  Closed = false
  End = (7056.31,5539.34,621.059)
  FilletRadius = 0
  Length = 2124.59
  MakeFace = true
  Points = (7) [(7078.94,5552.13,643.686),(7029,5550,693.627),(7029,5547.87,44),(7371,5545.74,44),(7371,5543.6,671),(7006.37,5541.47,671),(7056.31,5539.34,621.059)]
  Start = (7078.94,5552.13,643.686)
  Subdivisions = 0
  Support = -> [Structure011]
FEATURE [Part::FeaturePython] Rebar047  label="Хомуты011"  # Arch/BIM 110 (typed FeaturePython)
  Amount = 13
  AmountCheck = false
  Base = -> Wire011
  BentAngle = 135
  BentFactor = 4
  BottomCover = 40
  Diameter = 8
  Direction = (2e-16,1,0)
  Distance = 0
  FrontCover = 80
  HorizontalArea = 0
  Host = -> Structure011
  IfcType = 110
  LeftCover = 25
  Length = 2124.59
  Mark = Stirrup
  MoveBase = false
  MoveWithHost = false
  OffsetEnd = 84
  OffsetStart = 84
  PerimeterLength = 0
  PlacementList = 13 placements: arithmetic series from (1.86517e-14,84,0) step (1.07766e-13,485.333,0) to (1.31184e-12,5908,0)
  RebarShape = 3
  RightCover = 25
  Rounding = 2
  Spacing = 485.333
  TopCover = 25
  TotalLength = 27619.7
  TrueSpacing = 500
  VerticalArea = 0
FEATURE [Part::Box] Box012  label="Куб012"
  AttacherType = Attacher::AttachEngine3D
  Height = 700
  Length = 4450
  Width = 400
FEATURE [Part::FeaturePython] Structure012  label="Структура012"  # Arch/BIM 13 (typed FeaturePython)
  Base = -> Box012
  BaseMirror = false
  BaseOffsetX = 0
  BaseOffsetY = 0
  BasePerpendicularToTool = false
  BaseRotation = 0
  ComputedLength = 0
  FaceMaker = 0
  Height = 1000
  HorizontalArea = 1780000
  IfcData = attributes={"GlobalId": {"name": "GlobalId", "type": "IfcGloballyUniqueId", "is_enum": false, "enum_values": []}, "Description": {"... (+484 chars omitted),+1 more (map truncated)
  IfcType = 13
  Length = 0
  MoveBase = false
  MoveWithHost = false
  NodesOffset = 0
  Normal = (0,0,0)
  PerimeterLength = 9700
  Placement = pos=(6999,5148,0) rot=(0,0,1;0rad)
  PredefinedType = 0
  ToolOffsetFirst = 0
  ToolOffsetLast = 0
  VerticalArea = 6790000
  Width = 100
FEATURE [Sketcher::SketchObject] Sketch037
  FullyConstrained = false
  MapMode = 5
  Placement = pos=(6999,5148,0) rot=(1,0,0;1.5708rad)
  Support = -> [Structure012]
  sketch-geometry (1):
    g0: LineSegment StartX=0 StartY=56 StartZ=0 EndX=4450 EndY=56 EndZ=0
FEATURE [Part::FeaturePython] Rebar048  label="Нижняя_рабочая012"  # Arch/BIM 110 (typed FeaturePython)
  Amount = 3
  AmountCheck = true
  Base = -> Sketch037
  Cover = 50
  CoverAlong = Bottom Side
  Diameter = 12
  Direction = (0,0,0)
  Distance = 0
  FrontCover = 35
  HorizontalArea = 0
  Host = -> Structure012
  IfcType = 110
  LeftBottomCover = 0
  Length = 4450
  Mark = StraightRebar002
  MoveBase = false
  MoveWithHost = false
  OffsetEnd = 41
  OffsetStart = 41
  Orientation = Horizontal
  PerimeterLength = 0
  PlacementList = 3 placements: arithmetic series from (0,41,-9.10383e-15) step (0,159,-3.53051e-14) to (0,359,-7.9714e-14)
  RebarShape = 0
  RightTopCover = 0
  Rounding = 0
  Spacing = 159
  TotalLength = 13350
  TrueSpacing = 3
  VerticalArea = 0
FEATURE [Sketcher::SketchObject] Sketch038
  FullyConstrained = false
  MapMode = 5
  Placement = pos=(6999,5148,0) rot=(1,0,0;1.5708rad)
  Support = -> [Structure012]
  sketch-geometry (1):
    g0: LineSegment StartX=0 StartY=659 StartZ=0 EndX=4450 EndY=659 EndZ=0
FEATURE [Part::FeaturePython] Rebar049  label="Верхняя_рабочая012"  # Arch/BIM 110 (typed FeaturePython)
  Amount = 3
  AmountCheck = true
  Base = -> Sketch038
  Cover = 35
  CoverAlong = Top Side
  Diameter = 12
  Direction = (0,0,0)
  Distance = 0
  FrontCover = 35
  HorizontalArea = 0
  Host = -> Structure012
  IfcType = 110
  LeftBottomCover = 0
  Length = 4450
  Mark = StraightRebar002
  MoveBase = false
  MoveWithHost = false
  OffsetEnd = 41
  OffsetStart = 41
  Orientation = Horizontal
  PerimeterLength = 0
  PlacementList = 3 placements: arithmetic series from (0,41,-9.10383e-15) step (0,159,-3.53051e-14) to (0,359,-7.9714e-14)
  RebarShape = 0
  RightTopCover = 0
  Rounding = 0
  Spacing = 159
  TotalLength = 13350
  TrueSpacing = 3
  VerticalArea = 0
FEATURE [Part::Part2DObjectPython] Wire012  # Draft 2D object (typed FeaturePython)
  Area = 0
  ChamferSize = 0
  Closed = false
  End = (6988.34,5204.31,621.059)
  FilletRadius = 0
  Length = 2124.59
  MakeFace = true
  Points = (7) [(7001.13,5226.94,643.686),(6999,5177,693.627),(6996.87,5177,44),(6994.74,5519,44),(6992.6,5519,671),(6990.47,5154.37,671),(6988.34,5204.31,621.059)]
  Start = (7001.13,5226.94,643.686)
  Subdivisions = 0
  Support = -> [Structure012]
FEATURE [Part::FeaturePython] Rebar051  label="Хомуты012"  # Arch/BIM 110 (typed FeaturePython)
  Amount = 10
  AmountCheck = false
  Base = -> Wire012
  BentAngle = 135
  BentFactor = 4
  BottomCover = 40
  Diameter = 8
  Direction = (1,0,0)
  Distance = 0
  FrontCover = 80
  HorizontalArea = 0
  Host = -> Structure012
  IfcType = 110
  LeftCover = 25
  Length = 2124.59
  Mark = Stirrup
  MoveBase = false
  MoveWithHost = false
  OffsetEnd = 84
  OffsetStart = 84
  PerimeterLength = 0
  PlacementList = 10 placements: arithmetic series from (84,0,0) step (474.889,0,0) to (4358,0,0)
  RebarShape = 3
  RightCover = 25
  Rounding = 2
  Spacing = 474.889
  TopCover = 25
  TotalLength = 21245.9
  TrueSpacing = 500
  VerticalArea = 0
FEATURE [Part::Box] Box013  label="Куб013"
  AttacherType = Attacher::AttachEngine3D
  Height = 700
  Length = 1050
  Width = 400
FEATURE [Part::FeaturePython] Structure013  label="Структура013"  # Arch/BIM 13 (typed FeaturePython)
  Base = -> Box013
  BaseMirror = false
  BaseOffsetX = 0
  BaseOffsetY = 0
  BasePerpendicularToTool = false
  BaseRotation = 0
  ComputedLength = 0
  FaceMaker = 0
  Height = 1000
  HorizontalArea = 420000
  IfcData = attributes={"GlobalId": {"name": "GlobalId", "type": "IfcGloballyUniqueId", "is_enum": false, "enum_values": []}, "Description": {"... (+484 chars omitted),+1 more (map truncated)
  IfcType = 13
  Length = 0
  MoveBase = false
  MoveWithHost = false
  NodesOffset = 0
  Normal = (0,0,0)
  PerimeterLength = 2900
  Placement = pos=(7399,11552,0) rot=(0,0,1;1.5708rad)
  PredefinedType = 0
  ToolOffsetFirst = 0
  ToolOffsetLast = 0
  VerticalArea = 2030000
  Width = 100
FEATURE [Sketcher::SketchObject] Sketch040
  FullyConstrained = false
  MapMode = 5
  Placement = pos=(7399,11552,0) rot=(0.57735,0.57735,0.57735;2.0944rad)
  Support = -> [Structure013]
  sketch-geometry (1):
    g0: LineSegment StartX=0 StartY=56 StartZ=0 EndX=1050 EndY=56 EndZ=0
FEATURE [Part::FeaturePython] Rebar052  label="Нижняя_рабочая013"  # Arch/BIM 110 (typed FeaturePython)
  Amount = 3
  AmountCheck = true
  Base = -> Sketch040
  Cover = 50
  CoverAlong = Bottom Side
  Diameter = 12
  Direction = (0,0,0)
  Distance = 0
  FrontCover = 35
  HorizontalArea = 0
  Host = -> Structure013
  IfcType = 110
  LeftBottomCover = 0
  Length = 1050
  Mark = StraightRebar002
  MoveBase = false
  MoveWithHost = false
  OffsetEnd = 41
  OffsetStart = 41
  Orientation = Horizontal
  PerimeterLength = 0
  PlacementList = 3 placements: arithmetic series from (-41,4.55191e-15,4.55191e-15) step (-159,1.76525e-14,1.76525e-14) to (-359,3.9857e-14,3.9857e-14)
  RebarShape = 0
  RightTopCover = 0
  Rounding = 0
  Spacing = 159
  TotalLength = 3150
  TrueSpacing = 3
  VerticalArea = 0
FEATURE [Sketcher::SketchObject] Sketch041
  FullyConstrained = false
  MapMode = 5
  Placement = pos=(7399,11552,0) rot=(0.57735,0.57735,0.57735;2.0944rad)
  Support = -> [Structure013]
  sketch-geometry (1):
    g0: LineSegment StartX=0 StartY=659 StartZ=0 EndX=1050 EndY=659 EndZ=0
FEATURE [Part::FeaturePython] Rebar053  label="Верхняя_рабочая013"  # Arch/BIM 110 (typed FeaturePython)
  Amount = 3
  AmountCheck = true
  Base = -> Sketch041
  Cover = 35
  CoverAlong = Top Side
  Diameter = 12
  Direction = (0,0,0)
  Distance = 0
  FrontCover = 35
  HorizontalArea = 0
  Host = -> Structure013
  IfcType = 110
  LeftBottomCover = 0
  Length = 1050
  Mark = StraightRebar002
  MoveBase = false
  MoveWithHost = false
  OffsetEnd = 41
  OffsetStart = 41
  Orientation = Horizontal
  PerimeterLength = 0
  PlacementList = 3 placements: arithmetic series from (-41,4.55191e-15,4.55191e-15) step (-159,1.76525e-14,1.76525e-14) to (-359,3.9857e-14,3.9857e-14)
  RebarShape = 0
  RightTopCover = 0
  Rounding = 0
  Spacing = 159
  TotalLength = 3150
  TrueSpacing = 3
  VerticalArea = 0
FEATURE [Part::Part2DObjectPython] Wire013  # Draft 2D object (typed FeaturePython)
  Area = 0
  ChamferSize = 0
  Closed = false
  End = (7055.31,11541.3,621.059)
  FilletRadius = 0
  Length = 2124.59
  MakeFace = true
  Points = (7) [(7077.94,11554.1,643.686),(7028,11552,693.627),(7028,11549.9,44),(7370,11547.7,44),(7370,11545.6,671),(7005.37,11543.5,671),(7055.31,11541.3,621.059)]
  Start = (7077.94,11554.1,643.686)
  Subdivisions = 0
  Support = -> [Structure013]
FEATURE [Part::FeaturePython] Rebar055  label="Хомуты013"  # Arch/BIM 110 (typed FeaturePython)
  Amount = 4
  AmountCheck = false
  Base = -> Wire013
  BentAngle = 135
  BentFactor = 4
  BottomCover = 40
  Diameter = 8
  Direction = (2e-16,1,0)
  Distance = 0
  FrontCover = 80
  HorizontalArea = 0
  Host = -> Structure013
  IfcType = 110
  LeftCover = 25
  Length = 2124.59
  Mark = Stirrup
  MoveBase = false
  MoveWithHost = false
  OffsetEnd = 84
  OffsetStart = 84
  PerimeterLength = 0
  PlacementList = 4 placements: arithmetic series from (1.86517e-14,84,0) step (6.4689e-14,291.333,0) to (2.12719e-13,958,0)
  RebarShape = 3
  RightCover = 25
  Rounding = 2
  Spacing = 291.333
  TopCover = 25
  TotalLength = 8498.38
  TrueSpacing = 500
  VerticalArea = 0
FEATURE [Part::Box] Box014  label="Куб014"
  AttacherType = Attacher::AttachEngine3D
  Height = 700
  Length = 3150
  Width = 400
FEATURE [Part::FeaturePython] Structure014  label="Структура014"  # Arch/BIM 13 (typed FeaturePython)
  Base = -> Box014
  BaseMirror = false
  BaseOffsetX = 0
  BaseOffsetY = 0
  BasePerpendicularToTool = false
  BaseRotation = 0
  ComputedLength = 0
  FaceMaker = 0
  Height = 1000
  HorizontalArea = 1260000
  IfcData = attributes={"GlobalId": {"name": "GlobalId", "type": "IfcGloballyUniqueId", "is_enum": false, "enum_values": []}, "Description": {"... (+484 chars omitted),+1 more (map truncated)
  IfcType = 13
  Length = 0
  MoveBase = false
  MoveWithHost = false
  NodesOffset = 0
  Normal = (0,0,0)
  PerimeterLength = 7100
  Placement = pos=(3951,9451,0) rot=(0,0,1;1.5708rad)
  PredefinedType = 0
  ToolOffsetFirst = 0
  ToolOffsetLast = 0
  VerticalArea = 4970000
  Width = 100
FEATURE [Sketcher::SketchObject] Sketch043
  FullyConstrained = false
  MapMode = 5
  Placement = pos=(3951,9451,0) rot=(0.57735,0.57735,0.57735;2.0944rad)
  Support = -> [Structure014]
  sketch-geometry (1):
    g0: LineSegment StartX=0 StartY=56 StartZ=0 EndX=3150 EndY=56 EndZ=0
FEATURE [Part::FeaturePython] Rebar056  label="Нижняя_рабочая014"  # Arch/BIM 110 (typed FeaturePython)
  Amount = 3
  AmountCheck = true
  Base = -> Sketch043
  Cover = 50
  CoverAlong = Bottom Side
  Diameter = 12
  Direction = (0,0,0)
  Distance = 0
  FrontCover = 35
  HorizontalArea = 0
  Host = -> Structure014
  IfcType = 110
  LeftBottomCover = 0
  Length = 3150
  Mark = StraightRebar002
  MoveBase = false
  MoveWithHost = false
  OffsetEnd = 41
  OffsetStart = 41
  Orientation = Horizontal
  PerimeterLength = 0
  PlacementList = 3 placements: arithmetic series from (-41,4.55191e-15,4.55191e-15) step (-159,1.76525e-14,1.76525e-14) to (-359,3.9857e-14,3.9857e-14)
  RebarShape = 0
  RightTopCover = 0
  Rounding = 0
  Spacing = 159
  TotalLength = 9450
  TrueSpacing = 3
  VerticalArea = 0
FEATURE [Sketcher::SketchObject] Sketch044
  FullyConstrained = false
  MapMode = 5
  Placement = pos=(3951,9451,0) rot=(0.57735,0.57735,0.57735;2.0944rad)
  Support = -> [Structure014]
  sketch-geometry (1):
    g0: LineSegment StartX=0 StartY=659 StartZ=0 EndX=3150 EndY=659 EndZ=0
FEATURE [Part::FeaturePython] Rebar057  label="Верхняя_рабочая014"  # Arch/BIM 110 (typed FeaturePython)
  Amount = 3
  AmountCheck = true
  Base = -> Sketch044
  Cover = 35
  CoverAlong = Top Side
  Diameter = 12
  Direction = (0,0,0)
  Distance = 0
  FrontCover = 35
  HorizontalArea = 0
  Host = -> Structure014
  IfcType = 110
  LeftBottomCover = 0
  Length = 3150
  Mark = StraightRebar003
  MoveBase = false
  MoveWithHost = false
  OffsetEnd = 41
  OffsetStart = 41
  Orientation = Horizontal
  PerimeterLength = 0
  PlacementList = 3 placements: arithmetic series from (-41,4.55191e-15,4.55191e-15) step (-159,1.76525e-14,1.76525e-14) to (-359,3.9857e-14,3.9857e-14)
  RebarShape = 0
  RightTopCover = 0
  Rounding = 0
  Spacing = 159
  TotalLength = 9450
  TrueSpacing = 3
  VerticalArea = 0
FEATURE [Part::Part2DObjectPython] Wire014  # Draft 2D object (typed FeaturePython)
  Area = 0
  ChamferSize = 0
  Closed = false
  End = (3607.31,9440.34,621.059)
  FilletRadius = 0
  Length = 2124.59
  MakeFace = true
  Points = (7) [(3629.94,9453.13,643.686),(3580,9451,693.627),(3580,9448.87,44),(3922,9446.74,44),(3922,9444.6,671),(3557.37,9442.47,671),(3607.31,9440.34,621.059)]
  Start = (3629.94,9453.13,643.686)
  Subdivisions = 0
  Support = -> [Structure014]
FEATURE [Part::FeaturePython] Rebar059  label="Хомуты014"  # Arch/BIM 110 (typed FeaturePython)
  Amount = 8
  AmountCheck = false
  Base = -> Wire014
  BentAngle = 135
  BentFactor = 4
  BottomCover = 40
  Diameter = 8
  Direction = (2e-16,1,0)
  Distance = 0
  FrontCover = 80
  HorizontalArea = 0
  Host = -> Structure014
  IfcType = 110
  LeftCover = 25
  Length = 2124.59
  Mark = Stirrup
  MoveBase = false
  MoveWithHost = false
  OffsetEnd = 84
  OffsetStart = 84
  PerimeterLength = 0
  PlacementList = 8 placements: arithmetic series from (1.86517e-14,84,0) step (9.43372e-14,424.857,0) to (6.79012e-13,3058,0)
  RebarShape = 3
  RightCover = 25
  Rounding = 2
  Spacing = 424.857
  TopCover = 25
  TotalLength = 16996.8
  TrueSpacing = 500
  VerticalArea = 0
FEATURE [Part::Box] Box015  label="Куб015"
  AttacherType = Attacher::AttachEngine3D
  Height = 700
  Length = 1650
  Width = 400
FEATURE [Part::FeaturePython] Structure015  label="Структура015"  # Arch/BIM 13 (typed FeaturePython)
  Base = -> Box015
  BaseMirror = false
  BaseOffsetX = 0
  BaseOffsetY = 0
  BasePerpendicularToTool = false
  BaseRotation = 0
  ComputedLength = 0
  FaceMaker = 0
  Height = 1000
  HorizontalArea = 660000
  IfcData = attributes={"GlobalId": {"name": "GlobalId", "type": "IfcGloballyUniqueId", "is_enum": false, "enum_values": []}, "Description": {"... (+484 chars omitted),+1 more (map truncated)
  IfcType = 13
  Length = 0
  MoveBase = false
  MoveWithHost = false
  NodesOffset = 0
  Normal = (0,0,0)
  PerimeterLength = 4100
  Placement = pos=(1900,3448,0) rot=(0,0,1;0rad)
  PredefinedType = 0
  ToolOffsetFirst = 0
  ToolOffsetLast = 0
  VerticalArea = 2870000
  Width = 100
FEATURE [Sketcher::SketchObject] Sketch046
  FullyConstrained = false
  MapMode = 5
  Placement = pos=(1900,3448,0) rot=(1,0,0;1.5708rad)
  Support = -> [Structure015]
  sketch-geometry (1):
    g0: LineSegment StartX=0 StartY=56 StartZ=0 EndX=1650 EndY=56 EndZ=0
FEATURE [Part::FeaturePython] Rebar060  label="Нижняя_рабочая015"  # Arch/BIM 110 (typed FeaturePython)
  Amount = 3
  AmountCheck = true
  Base = -> Sketch046
  Cover = 50
  CoverAlong = Bottom Side
  Diameter = 12
  Direction = (0,0,0)
  Distance = 0
  FrontCover = 35
  HorizontalArea = 0
  Host = -> Structure015
  IfcType = 110
  LeftBottomCover = 0
  Length = 1650
  Mark = StraightRebar002
  MoveBase = false
  MoveWithHost = false
  OffsetEnd = 41
  OffsetStart = 41
  Orientation = Horizontal
  PerimeterLength = 0
  PlacementList = 3 placements: arithmetic series from (0,41,-9.10383e-15) step (0,159,-3.53051e-14) to (0,359,-7.9714e-14)
  RebarShape = 0
  RightTopCover = 0
  Rounding = 0
  Spacing = 159
  TotalLength = 4950
  TrueSpacing = 3
  VerticalArea = 0
FEATURE [Sketcher::SketchObject] Sketch047
  FullyConstrained = false
  MapMode = 5
  Placement = pos=(1900,3448,0) rot=(1,0,0;1.5708rad)
  Support = -> [Structure015]
  sketch-geometry (1):
    g0: LineSegment StartX=0 StartY=659 StartZ=0 EndX=1650 EndY=659 EndZ=0
FEATURE [Part::FeaturePython] Rebar061  label="Верхняя_рабочая015"  # Arch/BIM 110 (typed FeaturePython)
  Amount = 3
  AmountCheck = true
  Base = -> Sketch047
  Cover = 35
  CoverAlong = Top Side
  Diameter = 12
  Direction = (0,0,0)
  Distance = 0
  FrontCover = 35
  HorizontalArea = 0
  Host = -> Structure015
  IfcType = 110
  LeftBottomCover = 0
  Length = 1650
  Mark = StraightRebar003
  MoveBase = false
  MoveWithHost = false
  OffsetEnd = 41
  OffsetStart = 41
  Orientation = Horizontal
  PerimeterLength = 0
  PlacementList = 3 placements: arithmetic series from (0,41,-9.10383e-15) step (0,159,-3.53051e-14) to (0,359,-7.9714e-14)
  RebarShape = 0
  RightTopCover = 0
  Rounding = 0
  Spacing = 159
  TotalLength = 4950
  TrueSpacing = 3
  VerticalArea = 0
FEATURE [Part::Part2DObjectPython] Wire015  # Draft 2D object (typed FeaturePython)
  Area = 0
  ChamferSize = 0
  Closed = false
  End = (3539.34,3504.31,621.059)
  FilletRadius = 0
  Length = 2124.59
  MakeFace = true
  Points = (7) [(3552.13,3526.94,643.686),(3550,3477,693.627),(3547.87,3477,44),(3545.74,3819,44),(3543.6,3819,671),(3541.47,3454.37,671),(3539.34,3504.31,621.059)]
  Start = (3552.13,3526.94,643.686)
  Subdivisions = 0
  Support = -> [Structure015]
FEATURE [Part::FeaturePython] Rebar063  label="Хомуты015"  # Arch/BIM 110 (typed FeaturePython)
  Amount = 5
  AmountCheck = false
  Base = -> Wire015
  BentAngle = 135
  BentFactor = 4
  BottomCover = 40
  Diameter = 8
  Direction = (-1,0,0)
  Distance = 0
  FrontCover = 80
  HorizontalArea = 0
  Host = -> Structure015
  IfcType = 110
  LeftCover = 25
  Length = 2124.59
  Mark = Stirrup
  MoveBase = false
  MoveWithHost = false
  OffsetEnd = 84
  OffsetStart = 84
  PerimeterLength = 0
  PlacementList = 5 placements: arithmetic series from (-84,0,0) step (-368.5,0,0) to (-1558,0,0)
  RebarShape = 3
  RightCover = 25
  Rounding = 2
  Spacing = 368.5
  TopCover = 25
  TotalLength = 10623
  TrueSpacing = 500
  VerticalArea = 0
FEATURE [Spreadsheet::Sheet] RebarBillOfMaterial
  cells = A1='Member; B1='Mark; C1='No. of Rebars; D1='Diameter in mm; E1='Length in m/piece; F1='Total Length in m; F2='#8; G2='#12; A3='Структура; B3='Stirrup; C3='13; D3==8 mm; E3==2124.5940381749 mm; F3==27619.7224962737 mm; B4='StraightRebar; C4='3; D4==12 mm; E4==6000 mm; G4==18000 mm; B5='StraightRebar001; C5='3; D5==12 mm; E5==6000 mm; G5==18000 mm; A6='Структура001; B6='Stirrup; C6='13; D6==8 mm; E6==2124.5940381749 mm; F6==27619.7224962737 mm; B7='StraightRebar; C7='6; D7==12 mm; E7==5850 mm; G7==35100 mm; A8='Структура002; B8='Stirrup; C8='13; D8==8 mm; E8==2124.5940381749 mm; F8==27619.7224962737 mm; B9='StraightRebar; C9='6; D9==12 mm; E9==6000 mm; G9==36000 mm; A10='Структура003; B10='Stirrup; C10='13; D10==8 mm; E10==2124.5940381749 mm; F10==27619.7224962737 mm; B11='StraightRebar001; C11='6; D11==12 mm; E11==6000 mm; G11==36000 mm; A12='Структура004; B12='Stirrup; C12='13; D12==8 mm; E12==2124.5940381749 mm; F12==27619.7224962737 mm; B13='StraightRebar001; C13='3; D13==12 mm; E13==6000 mm; G13==18000 mm; B14='StraightRebar002; C14='3; D14==12 mm; E14==6000 mm; G14==18000 mm; A15='Структура005; B15='Stirrup; C15='13; D15==8 mm; E15==2124.5940381749 mm; F15==27619.7224962737 mm; B16='StraightRebar001; C16='6; D16==12 mm; E16==5850 mm; G16==35100 mm; A17='Структура006; B17='Stirrup; C17='13; D17==8 mm; E17==2124.5940381749 mm; F17==27619.7224962737 mm; B18='StraightRebar001; C18='6; D18==12 mm; E18==6000 mm; G18==36000 mm; A19='Структура007; B19='Stirrup; C19='13; D19==8 mm; E19==2124.5940381749 mm; F19==27619.7224962737 mm; B20='StraightRebar001; C20='3; D20==12 mm; E20==6000 mm; G20==18000 mm; B21='StraightRebar002; C21='3; D21==12 mm; E21==6000 mm; G21==18000 mm; A22='Структура008; B22='Stirrup; C22='13; D22==8 mm; E22==2124.5940381749 mm; F22==27619.7224962737 mm; B23='StraightRebar001; C23='6; D23==12 mm; E23==6000 mm; G23==36000 mm; A24='Структура009; B24='Stirrup; C24='4; D24==8 mm; E24==2124.5940381749 mm; F24==8498.37615269961 mm; B25='StraightRebar001; C25='6; D25==12 mm; E25==1500 mm; G25==9000 mm; A26='Структура010; B26='Stirrup; C26='13; D26==8 mm; E26==2124.5940381749 mm; F26==27619.7224962737 mm; B27='StraightRebar001; C27='6; D27==12 mm; E27==6000 mm; G27==36000 mm; A28='Структура011; B28='Stirrup; C28='13; D28==8 mm; E28==2124.5940381749 mm; F28==27619.7224962737 mm; B29='StraightRebar001; C29='6; D29==12 mm; E29==6000 mm; G29==36000 mm; A30='Структура012; B30='Stirrup; C30='10; D30==8 mm; E30==2124.5940381749 mm; F30==21245.940381749 mm; B31='StraightRebar002; C31='6; D31==12 mm; E31==4450 mm; G31==26700 mm; A32='Структура013; B32='Stirrup; C32='4; D32==8 mm; E32==2124.5940381749 mm; F32==8498.37615269961 mm; B33='StraightRebar002; C33='6; D33==12 mm; E33==1050 mm; G33==6300 mm; A34='Структура014; B34='Stirrup; C34='8; D34==8 mm; E34==2124.5940381749 mm; F34==16996.7523053992 mm; B35='StraightRebar002; C35='3; D35==12 mm; E35==3150 mm; G35==9450 mm; B36='StraightRebar003; C36='3; D36==12 mm; E36==3150 mm; G36==9450 mm; A37='Структура015; B37='Stirrup; C37='5; D37==8 mm; E37==2124.5940381749 mm; F37==10622.9701908745 mm; B38='StraightRebar002; +18 more cells
